FCSTD DOCUMENT  (FreeCAD 0.16R6712 (Git))
Label: parts
License: All rights reserved
LicenseURL: http://en.wikipedia.org/wiki/All_rights_reserved
objects: Part::Cylinder×41, Part::Cut×38, Part::Box×37, Part::MultiFuse×33, Part::Feature×31, Part::Fillet×30, Sketcher::SketchObject×22, PartDesign::Pad×21, Part::Chamfer×11, Part::Mirroring×6, Mesh::Feature×4, Part::Prism×3, Part::Thickness×2, App::DocumentObjectGroup×2, Part::FeaturePython×1, Part::Cone×1
note: 298 computed .brp shape members not serialized (recipe doc carries the construction recipe); baked Part::Feature solids carry a one-line shape summary decoded from their .brp

FEATURE [Part::Feature] Part__Feature  label="MEGAboard"
  shape: bbox 53.34 x 1.6 x 101.6 mm, 230 faces (baked)
FEATURE [Part::Feature] Part__Feature003  label="USB SHELL"
  Placement = pos=(-38.02,0.43,6.35) rot=(0,0,1;0rad)
  shape: bbox 13.78 x 15.2 x 16.51 mm, 218 faces (baked)
FEATURE [Part::MultiFuse] Fusion
  Placement = pos=(65,6,21) rot=(1,0,0;1.5708rad)
  Shapes = -> [Part__Feature,Part__Feature003]
FEATURE [Part::Box] Box  label="Cube"
  Height = 67
  Length = 84
  Placement = pos=(0,0,-3) rot=(0,0,1;0rad)
  Width = 120
FEATURE [Part::Box] Box001  label="Cube001"
  Height = 20
  Length = 20
  Placement = pos=(-20,0,0) rot=(0,0,-1;1.5708rad)
  Width = 300
FEATURE [Part::Box] Box002  label="Cube002"
  Height = 20
  Length = 20
  Placement = pos=(-20,0,50) rot=(0,0,-1;1.5708rad)
  Width = 300
FEATURE [Part::Box] Box003  label="Cube003"
  Height = 52
  Length = 54
  Placement = pos=(9,0,15) rot=(0,0,1;0rad)
  Width = 105
FEATURE [Part::Box] Box004  label="Cube004"
  Height = 20
  Length = 20
  Placement = pos=(-20,0,50) rot=(0,0,1;0rad)
  Width = 300
FEATURE [Part::Box] Box005  label="Cube005"
  Height = 20
  Length = 20
  Placement = pos=(-20,0,0) rot=(0,0,1;0rad)
  Width = 300
FEATURE [Sketcher::SketchObject] Sketch001
  Placement = pos=(0,0,100) rot=(0,0,1;0rad)
  sketch-geometry (28):
    g0: LineSegment StartX=82 StartY=111 StartZ=0 EndX=82 EndY=9 EndZ=0
    g1: LineSegment StartX=75 StartY=2 StartZ=0 EndX=9 EndY=2 EndZ=0
    g2: LineSegment StartX=2 StartY=9 StartZ=0 EndX=2 EndY=111 EndZ=0
    g3: ArcOfCircle CenterX=2 CenterY=118 CenterZ=0 NormalX=0 NormalY=0 NormalZ=1 Radius=7 StartAngle=4.71239 EndAngle=6.28319
    g4: LineSegment StartX=9 StartY=118 StartZ=0 EndX=75 EndY=118 EndZ=0
    g5: ArcOfCircle CenterX=2 CenterY=2 CenterZ=0 NormalX=0 NormalY=0 NormalZ=1 Radius=7 StartAngle=0 EndAngle=1.5708
    g6: ArcOfCircle CenterX=82 CenterY=2 CenterZ=0 NormalX=0 NormalY=0 NormalZ=1 Radius=7 StartAngle=1.5708 EndAngle=3.14159
    g7: ArcOfCircle CenterX=82 CenterY=118 CenterZ=0 NormalX=0 NormalY=0 NormalZ=1 Radius=7 StartAngle=3.14159 EndAngle=4.71239
    g8: LineSegment [constr] StartX=82 StartY=118 StartZ=0 EndX=75 EndY=118 EndZ=0
    g9: LineSegment [constr] StartX=82 StartY=118 StartZ=0 EndX=82 EndY=111 EndZ=0
    g10: LineSegment [constr] StartX=82 StartY=2 StartZ=0 EndX=82 EndY=9 EndZ=0
    g11: LineSegment [constr] StartX=82 StartY=2 StartZ=0 EndX=75 EndY=2 EndZ=0
    g12: LineSegment [constr] StartX=2 StartY=2 StartZ=0 EndX=2 EndY=9 EndZ=0
    g13: LineSegment [constr] StartX=2 StartY=2 StartZ=0 EndX=9 EndY=2 EndZ=0
    g14: LineSegment [constr] StartX=2 StartY=118 StartZ=0 EndX=2 EndY=111 EndZ=0
    g15: LineSegment [constr] StartX=2 StartY=118 StartZ=0 EndX=9 EndY=118 EndZ=0
    g16: Circle [constr] CenterX=4 CenterY=116 CenterZ=0 NormalX=0 NormalY=0 NormalZ=1 Radius=1.5
    g17: Circle [constr] CenterX=80 CenterY=116 CenterZ=0 NormalX=0 NormalY=0 NormalZ=1 Radius=1.5
    g18: Circle [constr] CenterX=80 CenterY=4 CenterZ=0 NormalX=0 NormalY=0 NormalZ=1 Radius=1.5
    g19: Circle [constr] CenterX=4 CenterY=4 CenterZ=0 NormalX=0 NormalY=0 NormalZ=1 Radius=1.5
    g20: LineSegment [constr] StartX=4 StartY=116 StartZ=0 EndX=80 EndY=116 EndZ=0
    g21: LineSegment [constr] StartX=80 StartY=116 StartZ=0 EndX=80 EndY=4 EndZ=0
    g22: LineSegment [constr] StartX=80 StartY=4 StartZ=0 EndX=4 EndY=4 EndZ=0
    g23: LineSegment [constr] StartX=4 StartY=4 StartZ=0 EndX=4 EndY=116 EndZ=0
    g24: LineSegment [constr] StartX=80 StartY=116 StartZ=0 EndX=80 EndY=118 EndZ=0
    g25: LineSegment [constr] StartX=80 StartY=116 StartZ=0 EndX=82 EndY=116 EndZ=0
    g26: LineSegment [constr] StartX=2 StartY=4 StartZ=0 EndX=4 EndY=4 EndZ=0
    g27: LineSegment [constr] StartX=4 StartY=4 StartZ=0 EndX=4 EndY=2 EndZ=0
  constraints (76):
    c: Horizontal(g1)
    c: Vertical(g0)
    c: Vertical(g2)
    c: Coincident(g4,g3)
    c: Coincident(g2,g3)
    c: Horizontal(g4)
    c: Coincident(g5,g2)
    c: Coincident(g5,g1)
    c: Coincident(g6,g0)
    c: Coincident(g6,g1)
    c: Coincident(g7,g4)
    c: Coincident(g7,g0)
    c: Coincident(g8,g7)
    c: Coincident(g8,g4)
    c: Coincident(g9,g7)
    c: Coincident(g9,g0)
    c: Coincident(g10,g6)
    c: Coincident(g10,g0)
    c: Vertical(g10)
    c: Coincident(g11,g6)
    c: Coincident(g11,g1)
    c: Horizontal(g11)
    c: Coincident(g12,g5)
    c: Coincident(g12,g2)
    c: Coincident(g13,g5)
    c: Coincident(g13,g1)
    c: Horizontal(g13)
    c: Horizontal(g8)
    c: Vertical(g9)
    c: Coincident(g14,g3)
    c: Coincident(g14,g2)
    c: Coincident(g15,g3)
    c: Coincident(g15,g3)
    c: Horizontal(g15)
    c: Vertical(g14)
    c: Distance(g3,g7) = 80
    c: Distance(g3,g5) = 116
    c: Vertical(g12)
    c: Equal(g3,g7)
    c: Equal(g7,g6)
    c: Equal(g6,g5)
    c: Radius(g5) = 7
    c: DistanceY(g-1,g5) = 2
    c: DistanceX(g-1,g5) = 2
    c: Coincident(g20,g21)
    c: Coincident(g21,g22)
    c: Coincident(g22,g23)
    c: Coincident(g23,g20)
    c: Horizontal(g20)
    c: Horizontal(g22)
    c: Vertical(g21)
    c: Vertical(g23)
    c: Coincident(g20,g16)
    c: Coincident(g21,g18)
    c: Coincident(g22,g19)
    c: Coincident(g20,g17)
    c: Radius(g17) = 1.5
    c: Equal(g17,g16)
    c: Equal(g17,g18)
    c: Equal(g17,g19)
    c: Coincident(g24,g17)
    c: PointOnObject(g24,g8)
    c: Coincident(g25,g17)
    c: PointOnObject(g25,g9)
    c: Horizontal(g25)
    c: Vertical(g24)
    c: PointOnObject(g26,g12)
    c: Coincident(g26,g19)
    c: Coincident(g26,g27)
    c: PointOnObject(g27,g13)
    c: Vertical(g27)
    c: Horizontal(g26)
    c: Equal(g26,g27)
    c: Equal(g27,g24)
    c: Equal(g24,g25)
    c: Distance(g26) = 2
FEATURE [Sketcher::SketchObject] Sketch002
  Placement = pos=(0,0,100) rot=(0,0,1;0rad)
  sketch-geometry (28):
    g0: LineSegment [constr] StartX=81 StartY=110 StartZ=0 EndX=81 EndY=10 EndZ=0
    g1: LineSegment [constr] StartX=74 StartY=3 StartZ=0 EndX=10 EndY=3 EndZ=0
    g2: LineSegment [constr] StartX=3 StartY=10 StartZ=0 EndX=3 EndY=110 EndZ=0
    g3: ArcOfCircle [constr] CenterX=3 CenterY=117 CenterZ=0 NormalX=0 NormalY=0 NormalZ=1 Radius=7 StartAngle=4.71239 EndAngle=6.28319
    g4: LineSegment [constr] StartX=10 StartY=117 StartZ=0 EndX=74 EndY=117 EndZ=0
    g5: ArcOfCircle [constr] CenterX=3 CenterY=3 CenterZ=0 NormalX=0 NormalY=0 NormalZ=1 Radius=7 StartAngle=0 EndAngle=1.5708
    g6: ArcOfCircle [constr] CenterX=81 CenterY=3 CenterZ=0 NormalX=0 NormalY=0 NormalZ=1 Radius=7 StartAngle=1.5708 EndAngle=3.14159
    g7: ArcOfCircle [constr] CenterX=81 CenterY=117 CenterZ=0 NormalX=0 NormalY=0 NormalZ=1 Radius=7 StartAngle=3.14159 EndAngle=4.71239
    g8: LineSegment [constr] StartX=81 StartY=117 StartZ=0 EndX=74 EndY=117 EndZ=0
    g9: LineSegment [constr] StartX=81 StartY=117 StartZ=0 EndX=81 EndY=110 EndZ=0
    g10: LineSegment [constr] StartX=81 StartY=3 StartZ=0 EndX=81 EndY=10 EndZ=0
    g11: LineSegment [constr] StartX=81 StartY=3 StartZ=0 EndX=74 EndY=3 EndZ=0
    g12: LineSegment [constr] StartX=3 StartY=3 StartZ=0 EndX=3 EndY=10 EndZ=0
    g13: LineSegment [constr] StartX=3 StartY=3 StartZ=0 EndX=10 EndY=3 EndZ=0
    g14: LineSegment [constr] StartX=3 StartY=117 StartZ=0 EndX=3 EndY=110 EndZ=0
    g15: LineSegment [constr] StartX=3 StartY=117 StartZ=0 EndX=10 EndY=117 EndZ=0
    g16: Circle CenterX=5 CenterY=115 CenterZ=0 NormalX=0 NormalY=0 NormalZ=1 Radius=1.5
    g17: Circle CenterX=79 CenterY=115 CenterZ=0 NormalX=0 NormalY=0 NormalZ=1 Radius=1.5
    g18: Circle CenterX=79 CenterY=5 CenterZ=0 NormalX=0 NormalY=0 NormalZ=1 Radius=1.5
    g19: Circle CenterX=5 CenterY=5 CenterZ=0 NormalX=0 NormalY=0 NormalZ=1 Radius=1.5
    g20: LineSegment [constr] StartX=5 StartY=115 StartZ=0 EndX=79 EndY=115 EndZ=0
    g21: LineSegment [constr] StartX=79 StartY=115 StartZ=0 EndX=79 EndY=5 EndZ=0
    g22: LineSegment [constr] StartX=79 StartY=5 StartZ=0 EndX=5 EndY=5 EndZ=0
    g23: LineSegment [constr] StartX=5 StartY=5 StartZ=0 EndX=5 EndY=115 EndZ=0
    g24: LineSegment [constr] StartX=79 StartY=115 StartZ=0 EndX=79 EndY=117 EndZ=0
    g25: LineSegment [constr] StartX=79 StartY=115 StartZ=0 EndX=81 EndY=115 EndZ=0
    g26: LineSegment [constr] StartX=3 StartY=5 StartZ=0 EndX=5 EndY=5 EndZ=0
    g27: LineSegment [constr] StartX=5 StartY=5 StartZ=0 EndX=5 EndY=3 EndZ=0
  constraints (76):
    c: Horizontal(g1)
    c: Vertical(g0)
    c: Vertical(g2)
    c: Coincident(g4,g3)
    c: Coincident(g2,g3)
    c: Horizontal(g4)
    c: Coincident(g5,g2)
    c: Coincident(g5,g1)
    c: Coincident(g6,g0)
    c: Coincident(g6,g1)
    c: Coincident(g7,g4)
    c: Coincident(g7,g0)
    c: Coincident(g8,g7)
    c: Coincident(g8,g4)
    c: Coincident(g9,g7)
    c: Coincident(g9,g0)
    c: Coincident(g10,g6)
    c: Coincident(g10,g0)
    c: Vertical(g10)
    c: Coincident(g11,g6)
    c: Coincident(g11,g1)
    c: Horizontal(g11)
    c: Coincident(g12,g5)
    c: Coincident(g12,g2)
    c: Coincident(g13,g5)
    c: Coincident(g13,g1)
    c: Horizontal(g13)
    c: Horizontal(g8)
    c: Vertical(g9)
    c: Coincident(g14,g3)
    c: Coincident(g14,g2)
    c: Coincident(g15,g3)
    c: Coincident(g15,g3)
    c: Horizontal(g15)
    c: Vertical(g14)
    c: Distance(g3,g7) = 78
    c: Distance(g3,g5) = 114
    c: Vertical(g12)
    c: Equal(g3,g7)
    c: Equal(g7,g6)
    c: Equal(g6,g5)
    c: Radius(g5) = 7
    c: DistanceY(g-1,g5) = 3
    c: DistanceX(g-1,g5) = 3
    c: Coincident(g20,g21)
    c: Coincident(g21,g22)
    c: Coincident(g22,g23)
    c: Coincident(g23,g20)
    c: Horizontal(g20)
    c: Horizontal(g22)
    c: Vertical(g21)
    c: Vertical(g23)
    c: Coincident(g20,g16)
    c: Coincident(g21,g18)
    c: Coincident(g22,g19)
    c: Coincident(g20,g17)
    c: Radius(g17) = 1.5
    c: Equal(g17,g16)
    c: Equal(g17,g18)
    c: Equal(g17,g19)
    c: Coincident(g24,g17)
    c: PointOnObject(g24,g8)
    c: Coincident(g25,g17)
    c: PointOnObject(g25,g9)
    c: Horizontal(g25)
    c: Vertical(g24)
    c: PointOnObject(g26,g12)
    c: Coincident(g26,g19)
    c: Coincident(g26,g27)
    c: PointOnObject(g27,g13)
    c: Vertical(g27)
    c: Horizontal(g26)
    c: Equal(g26,g27)
    c: Equal(g27,g24)
    c: Equal(g24,g25)
    c: Distance(g26) = 2
FEATURE [PartDesign::Pad] Pad
  Length = 101
  Length2 = 100
  Placement = pos=(0,0,100) rot=(0,0,1;0rad)
  Reversed = true
  Sketch = -> Sketch001
  Type = 0
FEATURE [Part::Cut] Cut
  Base = -> Box
  Tool = -> Pad
FEATURE [PartDesign::Pad] Pad001
  Length = 55
  Length2 = 100
  Placement = pos=(0,0,100) rot=(0,0,1;0rad)
  Reversed = true
  Sketch = -> Sketch002
  Type = 0
FEATURE [Part::Cut] Cut001
  Base = -> Cut
  Tool = -> Pad001
FEATURE [Part::Fillet] Fillet
  Base = -> Cut001
  Edges = 4 edges r=3: [Edge1,Edge3,Edge6,Edge23]
FEATURE [Part::Box] Box006  label="Cube006"
  Height = 14
  Length = 10
  Placement = pos=(80,11,3) rot=(0,0,1;0rad)
  Width = 32
FEATURE [Part::Fillet] Fillet001
  Base = -> Box006
  Edges = 4 edges r=1.5: [Edge9,Edge10,Edge11,Edge12]
FEATURE [Part::Fillet] Fillet002
  Base = -> Box006
  Edges = 4 edges r=1.5: [Edge9,Edge10,Edge11,Edge12]
  Placement = pos=(54,36,50) rot=(0,0,1;1.5708rad)
FEATURE [Part::Box] Box007  label="Cube007"
  Height = 12
  Length = 13
  Placement = pos=(20.5,-1,21) rot=(0,0,1;0rad)
  Width = 12
FEATURE [Part::Fillet] Fillet003
  Base = -> Box007
  Edges = 4 edges r=0.5: [Edge2,Edge4,Edge6,Edge8]
FEATURE [Sketcher::SketchObject] Sketch
  Placement = pos=(0,0,30) rot=(0,0,1;0rad)
  sketch-geometry (5):
    g0: Circle CenterX=29.4315 CenterY=72.043 CenterZ=0 NormalX=0 NormalY=0 NormalZ=1 Radius=1.5
    g1: Circle CenterX=57.3918 CenterY=72.0245 CenterZ=0 NormalX=0 NormalY=0 NormalZ=1 Radius=1.5
    g2: Circle CenterX=14.2201 CenterY=21.2508 CenterZ=0 NormalX=0 NormalY=0 NormalZ=1 Radius=1.5
    g3: Circle CenterX=62.4588 CenterY=102.502 CenterZ=0 NormalX=0 NormalY=0 NormalZ=1 Radius=1.5
    g4: Circle CenterX=62.4536 CenterY=19.9802 CenterZ=0 NormalX=0 NormalY=0 NormalZ=1 Radius=1.5
  constraints (5):
    c: Equal(g2,g4)
    c: Equal(g4,g1)
    c: Equal(g1,g3)
    c: Equal(g3,g0)
    c: Radius(g4) = 1.5
FEATURE [Sketcher::SketchObject] Sketch003
  Placement = pos=(0,0,-2) rot=(0,0,1;0rad)
  sketch-geometry (5):
    g0: Circle CenterX=29.4315 CenterY=72.043 CenterZ=0 NormalX=0 NormalY=0 NormalZ=1 Radius=3
    g1: Circle CenterX=57.3918 CenterY=72.0245 CenterZ=0 NormalX=0 NormalY=0 NormalZ=1 Radius=3
    g2: Circle CenterX=14.2201 CenterY=21.2508 CenterZ=0 NormalX=0 NormalY=0 NormalZ=1 Radius=3
    g3: Circle CenterX=62.4588 CenterY=102.502 CenterZ=0 NormalX=0 NormalY=0 NormalZ=1 Radius=3
    g4: Circle CenterX=62.4536 CenterY=19.9802 CenterZ=0 NormalX=0 NormalY=0 NormalZ=1 Radius=3
  constraints (5):
    c: Equal(g2,g4)
    c: Equal(g4,g1)
    c: Equal(g1,g3)
    c: Equal(g3,g0)
    c: Radius(g4) = 3
FEATURE [PartDesign::Pad] Pad002
  Length = 21.5
  Length2 = 100
  Placement = pos=(0,0,-2) rot=(0,0,1;0rad)
  Sketch = -> Sketch003
  Type = 0
FEATURE [Part::Box] Box008  label="Cube008"
  Height = 10
  Length = 6
  Placement = pos=(14,32,0) rot=(0,0,1;0rad)
  Width = 30
FEATURE [Part::Fillet] Fillet006
  Base = -> Box008
  Edges = 4 edges r=1: [Edge1,Edge3,Edge5,Edge7]
  Placement = pos=(0,0,-5) rot=(0,0,1;0rad)
FEATURE [Part::FeaturePython] Array  # Draft array (typed FeaturePython)
  Angle = 360
  ArrayType = 0
  Axis = (0,0,1)
  Base = -> Fillet006
  Center = (0,0,0)
  Fuse = false
  IntervalAxis = (0,0,0)
  IntervalX = (10,0,0)
  IntervalY = (0,1,0)
  IntervalZ = (0,0,0)
  NumberPolar = 1
  NumberX = 6
  NumberY = 1
  NumberZ = 1
FEATURE [PartDesign::Pad] Pad003
  Length = 20
  Length2 = 100
  Placement = pos=(0,0,30) rot=(0,0,1;0rad)
  Reversed = true
  Sketch = -> Sketch
  Type = 0
FEATURE [Part::Box] Box009  label="Cube009"
  Height = 3
  Length = 14
  Placement = pos=(-7,-17,-3) rot=(0,0,1;0rad)
  Width = 18
FEATURE [Part::Cylinder] Cylinder
  Angle = 360
  Height = 10
  Placement = pos=(0,-10,-5) rot=(0,0,1;0rad)
  Radius = 2.1
FEATURE [Part::Fillet] Fillet007
  Base = -> Box009
  Edges = 2 edges r=4: [Edge1,Edge5]
FEATURE [Part::Cut] Cut006
  Base = -> Fillet007
  Placement = pos=(16,0,0) rot=(0,0,1;0rad)
  Tool = -> Cylinder
FEATURE [Part::Cut] Cut007
  Base = -> Fillet007
  Placement = pos=(68,0,0) rot=(0,0,1;0rad)
  Tool = -> Cylinder
FEATURE [Part::Cut] Cut008
  Base = -> Fillet007
  Placement = pos=(0,40,0) rot=(0,0,-1;1.5708rad)
  Tool = -> Cylinder
FEATURE [Part::Cut] Cut009
  Base = -> Fillet007
  Placement = pos=(0,104,0) rot=(0,0,-1;1.5708rad)
  Tool = -> Cylinder
FEATURE [Part::Fillet] Fillet008
  Base = -> Box006
  Edges = 4 edges r=1.5: [Edge9,Edge10,Edge11,Edge12]
  Placement = pos=(54,36,0) rot=(0,0,1;1.5708rad)
FEATURE [Part::MultiFuse] Fusion001
  Shapes = -> [Fillet002,Fillet008,Fillet001]
FEATURE [Part::Cut] Cut010
  Base = -> Fillet
  Tool = -> Fusion001
FEATURE [Part::MultiFuse] Fusion002
  Shapes = -> [Cut007,Cut006,Cut008,Cut009]
FEATURE [Part::Cut] Cut011
  Base = -> Cut010
  Tool = -> Fillet003
FEATURE [Part::Cut] Cut012
  Base = -> Cut011
  Tool = -> Array
FEATURE [Part::MultiFuse] Fusion003
  Shapes = -> [Cut012,Pad002]
FEATURE [Part::Cut] Cut013
  Base = -> Fusion003
  Tool = -> Pad003
FEATURE [Part::Fillet] Fillet009
  Base = -> Cut013
  Edges = 8 edges r=1.5: [Edge106,Edge116,Edge118,Edge120,Edge123,Edge132,Edge135,Edge144]
FEATURE [Part::Fillet] Fillet010
  Base = -> Fillet009
  Edges = 5 edges r=3: [Edge92,Edge93,Edge142,Edge143,Edge144]
FEATURE [Part::MultiFuse] Fusion004
  Shapes = -> [Fillet010,Fusion002]
FEATURE [Sketcher::SketchObject] Sketch006
  Placement = pos=(0,0,1) rot=(0,0,1;0rad)
  sketch-geometry (35):
    g0: LineSegment StartX=-33.3333 StartY=25 StartZ=0 EndX=-16.6667 EndY=25 EndZ=0
    g1: LineSegment StartX=-16.6667 StartY=25 StartZ=0 EndX=-16.6667 EndY=-25 EndZ=0
    g2: LineSegment StartX=-16.6667 StartY=-25 StartZ=0 EndX=-33.3333 EndY=-25 EndZ=0
    g3: LineSegment StartX=-33.3333 StartY=-25 StartZ=0 EndX=-33.3333 EndY=25 EndZ=0
    g4: LineSegment StartX=-8.33333 StartY=-25 StartZ=0 EndX=8.33333 EndY=-25 EndZ=0
    g5: LineSegment StartX=8.33333 StartY=-25 StartZ=0 EndX=8.33333 EndY=-8.33333 EndZ=0
    g6: LineSegment StartX=8.33333 StartY=-8.33333 StartZ=0 EndX=16.6667 EndY=-8.33333 EndZ=0
    g7: LineSegment StartX=16.6667 StartY=-8.33333 StartZ=0 EndX=16.6667 EndY=-25 EndZ=0
    g8: LineSegment StartX=16.6667 StartY=-25 StartZ=0 EndX=33.3333 EndY=-25 EndZ=0
    g9: LineSegment StartX=33.3333 StartY=-25 StartZ=0 EndX=33.3333 EndY=25 EndZ=0
    g10: LineSegment StartX=16.6667 StartY=25 StartZ=0 EndX=16.6667 EndY=8.33333 EndZ=0
    g11: LineSegment StartX=8.33333 StartY=8.33333 StartZ=0 EndX=8.33333 EndY=25 EndZ=0
    g12: LineSegment StartX=8.33333 StartY=25 StartZ=0 EndX=-8.33333 EndY=25 EndZ=0
    g13: LineSegment [constr] StartX=16.6667 StartY=8.33333 StartZ=0 EndX=16.6667 EndY=-8.33333 EndZ=0
    g14: LineSegment StartX=8.33333 StartY=8.33333 StartZ=0 EndX=16.6667 EndY=8.33333 EndZ=0
    g15: LineSegment [constr] StartX=-16.6667 StartY=25 StartZ=0 EndX=-8.33333 EndY=25 EndZ=0
    g16: LineSegment [constr] StartX=8.33333 StartY=25 StartZ=0 EndX=16.6667 EndY=25 EndZ=0
    g17: LineSegment StartX=-8.33333 StartY=25 StartZ=0 EndX=-8.33333 EndY=8.33333 EndZ=0
    g18: LineSegment StartX=-8.33333 StartY=8.33333 StartZ=0 EndX=-12.5 EndY=8.33333 EndZ=0
    g19: LineSegment StartX=-12.5 StartY=8.33333 StartZ=0 EndX=-12.5 EndY=-8.33333 EndZ=0
    g20: LineSegment StartX=-12.5 StartY=-8.33333 StartZ=0 EndX=-8.33333 EndY=-8.33333 EndZ=0
    g21: LineSegment StartX=-8.33333 StartY=-8.33333 StartZ=0 EndX=-8.33333 EndY=-25 EndZ=0
    g22: LineSegment [constr] StartX=-8.33333 StartY=8.33333 StartZ=0 EndX=-8.33333 EndY=-8.33333 EndZ=0
    g23: LineSegment [constr] StartX=-16.6667 StartY=8.33333 StartZ=0 EndX=-12.5 EndY=8.33333 EndZ=0
    g24: LineSegment StartX=16.6667 StartY=25 StartZ=0 EndX=25 EndY=25 EndZ=0
    g25: LineSegment StartX=25 StartY=25 StartZ=0 EndX=33.3333 EndY=25 EndZ=0
    g26: LineSegment [constr] StartX=8.33333 StartY=8.33333 StartZ=0 EndX=8.33333 EndY=-8.33333 EndZ=0
    g27: LineSegment [constr] StartX=-16.6667 StartY=-25 StartZ=0 EndX=-8.33333 EndY=-25 EndZ=0
    g28: Circle CenterX=-25 CenterY=16.6667 CenterZ=0 NormalX=0 NormalY=0 NormalZ=1 Radius=4.16667
    g29: LineSegment [constr] StartX=-33.3333 StartY=25 StartZ=0 EndX=-25 EndY=16.6667 EndZ=0
    g30: LineSegment [constr] StartX=-25 StartY=16.6667 StartZ=0 EndX=-16.6667 EndY=25 EndZ=0
    g31: LineSegment [constr] StartX=-33.3333 StartY=16.6667 StartZ=0 EndX=-29.1667 EndY=16.6667 EndZ=0
    g32: LineSegment [constr] StartX=-29.1667 StartY=16.6667 StartZ=0 EndX=-25 EndY=16.6667 EndZ=0
    g33: LineSegment [constr] StartX=-33.3333 StartY=-25 StartZ=0 EndX=0 EndY=0 EndZ=0
    g34: LineSegment [constr] StartX=0 StartY=0 StartZ=0 EndX=33.3333 EndY=25 EndZ=0
  constraints (95):
    c: Coincident(g0,g1)
    c: Coincident(g1,g2)
    c: Coincident(g2,g3)
    c: Coincident(g3,g0)
    c: Horizontal(g0)
    c: Horizontal(g2)
    c: Vertical(g1)
    c: Vertical(g3)
    c: Horizontal(g4)
    c: Coincident(g4,g5)
    c: Vertical(g5)
    c: Coincident(g5,g6)
    c: Horizontal(g6)
    c: Coincident(g6,g7)
    c: Vertical(g7)
    c: Coincident(g7,g8)
    c: Horizontal(g8)
    c: Coincident(g8,g9)
    c: Vertical(g9)
    c: Vertical(g11)
    c: Coincident(g11,g12)
    c: Horizontal(g12)
    c: Vertical(g10)
    c: Coincident(g13,g6)
    c: Vertical(g13)
    c: Coincident(g13,g10)
    c: Equal(g11,g12)
    c: Equal(g12,g0)
    c: Coincident(g14,g10)
    c: Horizontal(g14)
    c: Coincident(g11,g14)
    c: Coincident(g15,g0)
    c: Equal(g15,g14)
    c: Horizontal(g15)
    c: Coincident(g16,g11)
    c: Horizontal(g16)
    c: Coincident(g12,g17)
    c: Vertical(g17)
    c: Coincident(g17,g18)
    c: Horizontal(g18)
    c: Coincident(g18,g19)
    c: Vertical(g19)
    c: Coincident(g19,g20)
    c: Coincident(g20,g21)
    c: Coincident(g21,g4)
    c: Vertical(g21)
    c: Horizontal(g20)
    c: Coincident(g22,g17)
    c: Coincident(g22,g20)
    c: Vertical(g22)
    c: PointOnObject(g23,g1)
    c: Coincident(g23,g18)
    c: Horizontal(g23)
    c: Equal(g18,g23)
    c: Coincident(g10,g24)
    c: Horizontal(g24)
    c: Coincident(g24,g25)
    c: Coincident(g25,g9)
    c: Horizontal(g25)
    c: Equal(g16,g24)
    c: Equal(g24,g25)
    c: Coincident(g10,g16)
    c: Coincident(g15,g12)
    c: Equal(g17,g11)
    c: Equal(g7,g5)
    c: Equal(g21,g17)
    c: Coincident(g26,g11)
    c: Coincident(g26,g5)
    c: Vertical(g26)
    c: Coincident(g27,g1)
    c: Coincident(g27,g4)
    c: Horizontal(g27)
    c: Equal(g19,g17)
    c: Equal(g26,g11)
    c: Coincident(g29,g0)
    c: Coincident(g29,g28)
    c: Coincident(g30,g28)
    c: Coincident(g30,g0)
    c: Perpendicular(g30,g29)
    c: Equal(g30,g29)
    c: PointOnObject(g31,g3)
    c: PointOnObject(g31,g28)
    c: Coincident(g32,g31)
    c: Coincident(g32,g28)
    c: Horizontal(g31)
    c: Horizontal(g32)
    c: Equal(g31,g32)
    c: Equal(g4,g8)
    c: Distance(g3) = 50
    c: Coincident(g33,g2)
    c: Coincident(g33,g-1)
    c: Coincident(g34,g-1)
    c: Coincident(g34,g9)
    c: Parallel(g34,g33)
    c: Equal(g34,g33)
FEATURE [Sketcher::SketchObject] Sketch007
  sketch-geometry (16):
    g0: LineSegment StartX=-90 StartY=-35 StartZ=0 EndX=90 EndY=-35 EndZ=0
    g1: LineSegment StartX=90 StartY=-35 StartZ=0 EndX=90 EndY=35 EndZ=0
    g2: LineSegment StartX=90 StartY=35 StartZ=0 EndX=-90 EndY=35 EndZ=0
    g3: LineSegment StartX=-90 StartY=35 StartZ=0 EndX=-90 EndY=-35 EndZ=0
    g4: Circle CenterX=-80 CenterY=25 CenterZ=0 NormalX=0 NormalY=0 NormalZ=1 Radius=2
    g5: Circle CenterX=-80 CenterY=-25 CenterZ=0 NormalX=0 NormalY=0 NormalZ=1 Radius=2
    g6: Circle CenterX=80 CenterY=25 CenterZ=0 NormalX=0 NormalY=0 NormalZ=1 Radius=2
    g7: Circle CenterX=80 CenterY=-25 CenterZ=0 NormalX=0 NormalY=0 NormalZ=1 Radius=2
    g8: LineSegment [constr] StartX=80 StartY=25 StartZ=0 EndX=-80 EndY=25 EndZ=0
    g9: LineSegment [constr] StartX=-80 StartY=25 StartZ=0 EndX=-80 EndY=-25 EndZ=0
    g10: LineSegment [constr] StartX=-80 StartY=-25 StartZ=0 EndX=80 EndY=-25 EndZ=0
    g11: LineSegment [constr] StartX=80 StartY=-25 StartZ=0 EndX=80 EndY=25 EndZ=0
    g12: LineSegment [constr] StartX=-80 StartY=-25 StartZ=0 EndX=0 EndY=0 EndZ=0
    g13: LineSegment [constr] StartX=0 StartY=0 StartZ=0 EndX=80 EndY=25 EndZ=0
    g14: LineSegment [constr] StartX=80 StartY=25 StartZ=0 EndX=80 EndY=35 EndZ=0
    g15: LineSegment [constr] StartX=80 StartY=25 StartZ=0 EndX=90 EndY=25 EndZ=0
  constraints (40):
    c: Coincident(g0,g1)
    c: Coincident(g1,g2)
    c: Coincident(g2,g3)
    c: Coincident(g3,g0)
    c: Horizontal(g0)
    c: Vertical(g1)
    c: Distance(g3) = 70
    c: Distance(g2) = 180
    c: Radius(g4) = 2
    c: Equal(g4,g5)
    c: Equal(g4,g6)
    c: Equal(g4,g7)
    c: Coincident(g8,g9)
    c: Coincident(g9,g10)
    c: Coincident(g10,g11)
    c: Coincident(g11,g8)
    c: Horizontal(g8)
    c: Horizontal(g10)
    c: Vertical(g9)
    c: Vertical(g11)
    c: Coincident(g8,g6)
    c: Coincident(g9,g5)
    c: Coincident(g4,g8)
    c: Coincident(g7,g10)
    c: Symmetric(g2,g1,g-2)
    c: Symmetric(g0,g2,g-1)
    c: Coincident(g12,g5)
    c: Coincident(g12,g-1)
    c: Coincident(g13,g-1)
    c: Coincident(g13,g6)
    c: Equal(g13,g12)
    c: Parallel(g12,g13)
    c: Distance(g11) = 50
    c: Coincident(g14,g6)
    c: PointOnObject(g14,g2)
    c: Vertical(g14)
    c: Coincident(g15,g6)
    c: PointOnObject(g15,g1)
    c: Horizontal(g15)
    c: Equal(g14,g15)
FEATURE [PartDesign::Pad] Pad004
  Length = 3
  Length2 = 100
  Sketch = -> Sketch007
  Type = 0
FEATURE [PartDesign::Pad] Pad005
  Length = 10
  Length2 = 100
  Placement = pos=(0,0,1) rot=(0,0,1;0rad)
  Sketch = -> Sketch006
  Type = 0
FEATURE [Part::Fillet] Fillet011
  Base = -> Pad004
  Edges = 4 edges r=3: [Edge1,Edge2,Edge5,Edge8]
FEATURE [Sketcher::SketchObject] Sketch008
  Placement = pos=(0,0,1.5) rot=(0,0,1;0rad)
  sketch-geometry (35):
    g0: LineSegment StartX=-33.3333 StartY=25 StartZ=0 EndX=-16.6667 EndY=25 EndZ=0
    g1: LineSegment StartX=-16.6667 StartY=25 StartZ=0 EndX=-16.6667 EndY=-25 EndZ=0
    g2: LineSegment StartX=-16.6667 StartY=-25 StartZ=0 EndX=-33.3333 EndY=-25 EndZ=0
    g3: LineSegment StartX=-33.3333 StartY=-25 StartZ=0 EndX=-33.3333 EndY=25 EndZ=0
    g4: LineSegment StartX=-8.33333 StartY=-25 StartZ=0 EndX=8.33333 EndY=-25 EndZ=0
    g5: LineSegment StartX=8.33333 StartY=-25 StartZ=0 EndX=8.33333 EndY=-8.33333 EndZ=0
    g6: LineSegment StartX=8.33333 StartY=-8.33333 StartZ=0 EndX=16.6667 EndY=-8.33333 EndZ=0
    g7: LineSegment StartX=16.6667 StartY=-8.33333 StartZ=0 EndX=16.6667 EndY=-25 EndZ=0
    g8: LineSegment StartX=16.6667 StartY=-25 StartZ=0 EndX=33.3333 EndY=-25 EndZ=0
    g9: LineSegment StartX=33.3333 StartY=-25 StartZ=0 EndX=33.3333 EndY=25 EndZ=0
    g10: LineSegment StartX=16.6667 StartY=25 StartZ=0 EndX=16.6667 EndY=8.33333 EndZ=0
    g11: LineSegment StartX=8.33333 StartY=8.33333 StartZ=0 EndX=8.33333 EndY=25 EndZ=0
    g12: LineSegment StartX=8.33333 StartY=25 StartZ=0 EndX=-8.33333 EndY=25 EndZ=0
    g13: LineSegment [constr] StartX=16.6667 StartY=8.33333 StartZ=0 EndX=16.6667 EndY=-8.33333 EndZ=0
    g14: LineSegment StartX=8.33333 StartY=8.33333 StartZ=0 EndX=16.6667 EndY=8.33333 EndZ=0
    g15: LineSegment [constr] StartX=-16.6667 StartY=25 StartZ=0 EndX=-8.33333 EndY=25 EndZ=0
    g16: LineSegment [constr] StartX=8.33333 StartY=25 StartZ=0 EndX=16.6667 EndY=25 EndZ=0
    g17: LineSegment StartX=-8.33333 StartY=25 StartZ=0 EndX=-8.33333 EndY=8.33333 EndZ=0
    g18: LineSegment StartX=-8.33333 StartY=8.33333 StartZ=0 EndX=-12.5 EndY=8.33333 EndZ=0
    g19: LineSegment StartX=-12.5 StartY=8.33333 StartZ=0 EndX=-12.5 EndY=-8.33333 EndZ=0
    g20: LineSegment StartX=-12.5 StartY=-8.33333 StartZ=0 EndX=-8.33333 EndY=-8.33333 EndZ=0
    g21: LineSegment StartX=-8.33333 StartY=-8.33333 StartZ=0 EndX=-8.33333 EndY=-25 EndZ=0
    g22: LineSegment [constr] StartX=-8.33333 StartY=8.33333 StartZ=0 EndX=-8.33333 EndY=-8.33333 EndZ=0
    g23: LineSegment [constr] StartX=-16.6667 StartY=8.33333 StartZ=0 EndX=-12.5 EndY=8.33333 EndZ=0
    g24: LineSegment StartX=16.6667 StartY=25 StartZ=0 EndX=25 EndY=25 EndZ=0
    g25: LineSegment StartX=25 StartY=25 StartZ=0 EndX=33.3333 EndY=25 EndZ=0
    g26: LineSegment [constr] StartX=8.33333 StartY=8.33333 StartZ=0 EndX=8.33333 EndY=-8.33333 EndZ=0
    g27: LineSegment [constr] StartX=-16.6667 StartY=-25 StartZ=0 EndX=-8.33333 EndY=-25 EndZ=0
    g28: Circle CenterX=-25 CenterY=16.6667 CenterZ=0 NormalX=0 NormalY=0 NormalZ=1 Radius=4.16667
    g29: LineSegment [constr] StartX=-33.3333 StartY=25 StartZ=0 EndX=-25 EndY=16.6667 EndZ=0
    g30: LineSegment [constr] StartX=-25 StartY=16.6667 StartZ=0 EndX=-16.6667 EndY=25 EndZ=0
    g31: LineSegment [constr] StartX=-33.3333 StartY=16.6667 StartZ=0 EndX=-29.1667 EndY=16.6667 EndZ=0
    g32: LineSegment [constr] StartX=-29.1667 StartY=16.6667 StartZ=0 EndX=-25 EndY=16.6667 EndZ=0
    g33: LineSegment [constr] StartX=-33.3333 StartY=-25 StartZ=0 EndX=0 EndY=0 EndZ=0
    g34: LineSegment [constr] StartX=0 StartY=0 StartZ=0 EndX=33.3333 EndY=25 EndZ=0
  constraints (95):
    c: Coincident(g0,g1)
    c: Coincident(g1,g2)
    c: Coincident(g2,g3)
    c: Coincident(g3,g0)
    c: Horizontal(g0)
    c: Horizontal(g2)
    c: Vertical(g1)
    c: Vertical(g3)
    c: Horizontal(g4)
    c: Coincident(g4,g5)
    c: Vertical(g5)
    c: Coincident(g5,g6)
    c: Horizontal(g6)
    c: Coincident(g6,g7)
    c: Vertical(g7)
    c: Coincident(g7,g8)
    c: Horizontal(g8)
    c: Coincident(g8,g9)
    c: Vertical(g9)
    c: Vertical(g11)
    c: Coincident(g11,g12)
    c: Horizontal(g12)
    c: Vertical(g10)
    c: Coincident(g13,g6)
    c: Vertical(g13)
    c: Coincident(g13,g10)
    c: Equal(g11,g12)
    c: Equal(g12,g0)
    c: Coincident(g14,g10)
    c: Horizontal(g14)
    c: Coincident(g11,g14)
    c: Coincident(g15,g0)
    c: Equal(g15,g14)
    c: Horizontal(g15)
    c: Coincident(g16,g11)
    c: Horizontal(g16)
    c: Coincident(g12,g17)
    c: Vertical(g17)
    c: Coincident(g17,g18)
    c: Horizontal(g18)
    c: Coincident(g18,g19)
    c: Vertical(g19)
    c: Coincident(g19,g20)
    c: Coincident(g20,g21)
    c: Coincident(g21,g4)
    c: Vertical(g21)
    c: Horizontal(g20)
    c: Coincident(g22,g17)
    c: Coincident(g22,g20)
    c: Vertical(g22)
    c: PointOnObject(g23,g1)
    c: Coincident(g23,g18)
    c: Horizontal(g23)
    c: Equal(g18,g23)
    c: Coincident(g10,g24)
    c: Horizontal(g24)
    c: Coincident(g24,g25)
    c: Coincident(g25,g9)
    c: Horizontal(g25)
    c: Equal(g16,g24)
    c: Equal(g24,g25)
    c: Coincident(g10,g16)
    c: Coincident(g15,g12)
    c: Equal(g17,g11)
    c: Equal(g7,g5)
    c: Equal(g21,g17)
    c: Coincident(g26,g11)
    c: Coincident(g26,g5)
    c: Vertical(g26)
    c: Coincident(g27,g1)
    c: Coincident(g27,g4)
    c: Horizontal(g27)
    c: Equal(g19,g17)
    c: Equal(g26,g11)
    c: Coincident(g29,g0)
    c: Coincident(g29,g28)
    c: Coincident(g30,g28)
    c: Coincident(g30,g0)
    c: Perpendicular(g30,g29)
    c: Equal(g30,g29)
    c: PointOnObject(g31,g3)
    c: PointOnObject(g31,g28)
    c: Coincident(g32,g31)
    c: Coincident(g32,g28)
    c: Horizontal(g31)
    c: Horizontal(g32)
    c: Equal(g31,g32)
    c: Equal(g4,g8)
    c: Distance(g3) = 50
    c: Coincident(g33,g2)
    c: Coincident(g33,g-1)
    c: Coincident(g34,g-1)
    c: Coincident(g34,g9)
    c: Parallel(g34,g33)
    c: Equal(g34,g33)
FEATURE [PartDesign::Pad] Pad006
  Length = 2
  Length2 = 100
  Placement = pos=(0,0,1.5) rot=(0,0,1;0rad)
  Sketch = -> Sketch008
  Type = 0
FEATURE [Sketcher::SketchObject] Sketch009
  Placement = pos=(0,0,100) rot=(0,0,1;0rad)
  sketch-geometry (28):
    g0: LineSegment [constr] StartX=81 StartY=110 StartZ=0 EndX=81 EndY=10 EndZ=0
    g1: LineSegment [constr] StartX=74 StartY=3 StartZ=0 EndX=10 EndY=3 EndZ=0
    g2: LineSegment [constr] StartX=3 StartY=10 StartZ=0 EndX=3 EndY=110 EndZ=0
    g3: ArcOfCircle [constr] CenterX=3 CenterY=117 CenterZ=0 NormalX=0 NormalY=0 NormalZ=1 Radius=7 StartAngle=4.71239 EndAngle=6.28319
    g4: LineSegment [constr] StartX=10 StartY=117 StartZ=0 EndX=74 EndY=117 EndZ=0
    g5: ArcOfCircle [constr] CenterX=3 CenterY=3 CenterZ=0 NormalX=0 NormalY=0 NormalZ=1 Radius=7 StartAngle=0 EndAngle=1.5708
    g6: ArcOfCircle [constr] CenterX=81 CenterY=3 CenterZ=0 NormalX=0 NormalY=0 NormalZ=1 Radius=7 StartAngle=1.5708 EndAngle=3.14159
    g7: ArcOfCircle [constr] CenterX=81 CenterY=117 CenterZ=0 NormalX=0 NormalY=0 NormalZ=1 Radius=7 StartAngle=3.14159 EndAngle=4.71239
    g8: LineSegment [constr] StartX=81 StartY=117 StartZ=0 EndX=74 EndY=117 EndZ=0
    g9: LineSegment [constr] StartX=81 StartY=117 StartZ=0 EndX=81 EndY=110 EndZ=0
    g10: LineSegment [constr] StartX=81 StartY=3 StartZ=0 EndX=81 EndY=10 EndZ=0
    g11: LineSegment [constr] StartX=81 StartY=3 StartZ=0 EndX=74 EndY=3 EndZ=0
    g12: LineSegment [constr] StartX=3 StartY=3 StartZ=0 EndX=3 EndY=10 EndZ=0
    g13: LineSegment [constr] StartX=3 StartY=3 StartZ=0 EndX=10 EndY=3 EndZ=0
    g14: LineSegment [constr] StartX=3 StartY=117 StartZ=0 EndX=3 EndY=110 EndZ=0
    g15: LineSegment [constr] StartX=3 StartY=117 StartZ=0 EndX=10 EndY=117 EndZ=0
    g16: Circle CenterX=5 CenterY=115 CenterZ=0 NormalX=0 NormalY=0 NormalZ=1 Radius=1.65
    g17: Circle CenterX=79 CenterY=115 CenterZ=0 NormalX=0 NormalY=0 NormalZ=1 Radius=1.65
    g18: Circle CenterX=79 CenterY=5 CenterZ=0 NormalX=0 NormalY=0 NormalZ=1 Radius=1.65
    g19: Circle CenterX=5 CenterY=5 CenterZ=0 NormalX=0 NormalY=0 NormalZ=1 Radius=1.65
    g20: LineSegment [constr] StartX=5 StartY=115 StartZ=0 EndX=79 EndY=115 EndZ=0
    g21: LineSegment [constr] StartX=79 StartY=115 StartZ=0 EndX=79 EndY=5 EndZ=0
    g22: LineSegment [constr] StartX=79 StartY=5 StartZ=0 EndX=5 EndY=5 EndZ=0
    g23: LineSegment [constr] StartX=5 StartY=5 StartZ=0 EndX=5 EndY=115 EndZ=0
    g24: LineSegment [constr] StartX=79 StartY=115 StartZ=0 EndX=79 EndY=117 EndZ=0
    g25: LineSegment [constr] StartX=79 StartY=115 StartZ=0 EndX=81 EndY=115 EndZ=0
    g26: LineSegment [constr] StartX=3 StartY=5 StartZ=0 EndX=5 EndY=5 EndZ=0
    g27: LineSegment [constr] StartX=5 StartY=5 StartZ=0 EndX=5 EndY=3 EndZ=0
  constraints (76):
    c: Horizontal(g1)
    c: Vertical(g0)
    c: Vertical(g2)
    c: Coincident(g4,g3)
    c: Coincident(g2,g3)
    c: Horizontal(g4)
    c: Coincident(g5,g2)
    c: Coincident(g5,g1)
    c: Coincident(g6,g0)
    c: Coincident(g6,g1)
    c: Coincident(g7,g4)
    c: Coincident(g7,g0)
    c: Coincident(g8,g7)
    c: Coincident(g8,g4)
    c: Coincident(g9,g7)
    c: Coincident(g9,g0)
    c: Coincident(g10,g6)
    c: Coincident(g10,g0)
    c: Vertical(g10)
    c: Coincident(g11,g6)
    c: Coincident(g11,g1)
    c: Horizontal(g11)
    c: Coincident(g12,g5)
    c: Coincident(g12,g2)
    c: Coincident(g13,g5)
    c: Coincident(g13,g1)
    c: Horizontal(g13)
    c: Horizontal(g8)
    c: Vertical(g9)
    c: Coincident(g14,g3)
    c: Coincident(g14,g2)
    c: Coincident(g15,g3)
    c: Coincident(g15,g3)
    c: Horizontal(g15)
    c: Vertical(g14)
    c: Distance(g3,g7) = 78
    c: Distance(g3,g5) = 114
    c: Vertical(g12)
    c: Equal(g3,g7)
    c: Equal(g7,g6)
    c: Equal(g6,g5)
    c: Radius(g5) = 7
    c: DistanceY(g-1,g5) = 3
    c: DistanceX(g-1,g5) = 3
    c: Coincident(g20,g21)
    c: Coincident(g21,g22)
    c: Coincident(g22,g23)
    c: Coincident(g23,g20)
    c: Horizontal(g20)
    c: Horizontal(g22)
    c: Vertical(g21)
    c: Vertical(g23)
    c: Coincident(g20,g16)
    c: Coincident(g21,g18)
    c: Coincident(g22,g19)
    c: Coincident(g20,g17)
    c: Radius(g17) = 1.65
    c: Equal(g17,g16)
    c: Equal(g17,g18)
    c: Equal(g17,g19)
    c: Coincident(g24,g17)
    c: PointOnObject(g24,g8)
    c: Coincident(g25,g17)
    c: PointOnObject(g25,g9)
    c: Horizontal(g25)
    c: Vertical(g24)
    c: PointOnObject(g26,g12)
    c: Coincident(g26,g19)
    c: Coincident(g26,g27)
    c: PointOnObject(g27,g13)
    c: Vertical(g27)
    c: Horizontal(g26)
    c: Equal(g26,g27)
    c: Equal(g27,g24)
    c: Equal(g24,g25)
    c: Distance(g26) = 2
FEATURE [PartDesign::Pad] Pad007
  Length = 55
  Length2 = 100
  Placement = pos=(0,0,100) rot=(0,0,1;0rad)
  Reversed = true
  Sketch = -> Sketch009
  Type = 0
FEATURE [Part::Box] Box010  label="Cube010"
  Height = 5
  Length = 84
  Placement = pos=(0,0,64) rot=(0,0,1;0rad)
  Width = 120
FEATURE [Part::Fillet] Fillet012
  Base = -> Box010
  Edges = 4 edges r=3: [Edge1,Edge3,Edge5,Edge7]
FEATURE [Sketcher::SketchObject] Sketch010
  Placement = pos=(0,0,68) rot=(0,0,1;0rad)
  sketch-geometry (28):
    g0: LineSegment StartX=82 StartY=111 StartZ=0 EndX=82 EndY=9 EndZ=0
    g1: LineSegment StartX=75 StartY=2 StartZ=0 EndX=9 EndY=2 EndZ=0
    g2: LineSegment StartX=2 StartY=9 StartZ=0 EndX=2 EndY=111 EndZ=0
    g3: ArcOfCircle CenterX=2 CenterY=118 CenterZ=0 NormalX=0 NormalY=0 NormalZ=1 Radius=7 StartAngle=4.71239 EndAngle=6.28319
    g4: LineSegment StartX=9 StartY=118 StartZ=0 EndX=75 EndY=118 EndZ=0
    g5: ArcOfCircle CenterX=2 CenterY=2 CenterZ=0 NormalX=0 NormalY=0 NormalZ=1 Radius=7 StartAngle=0 EndAngle=1.5708
    g6: ArcOfCircle CenterX=82 CenterY=2 CenterZ=0 NormalX=0 NormalY=0 NormalZ=1 Radius=7 StartAngle=1.5708 EndAngle=3.14159
    g7: ArcOfCircle CenterX=82 CenterY=118 CenterZ=0 NormalX=0 NormalY=0 NormalZ=1 Radius=7 StartAngle=3.14159 EndAngle=4.71239
    g8: LineSegment [constr] StartX=82 StartY=118 StartZ=0 EndX=75 EndY=118 EndZ=0
    g9: LineSegment [constr] StartX=82 StartY=118 StartZ=0 EndX=82 EndY=111 EndZ=0
    g10: LineSegment [constr] StartX=82 StartY=2 StartZ=0 EndX=82 EndY=9 EndZ=0
    g11: LineSegment [constr] StartX=82 StartY=2 StartZ=0 EndX=75 EndY=2 EndZ=0
    g12: LineSegment [constr] StartX=2 StartY=2 StartZ=0 EndX=2 EndY=9 EndZ=0
    g13: LineSegment [constr] StartX=2 StartY=2 StartZ=0 EndX=9 EndY=2 EndZ=0
    g14: LineSegment [constr] StartX=2 StartY=118 StartZ=0 EndX=2 EndY=111 EndZ=0
    g15: LineSegment [constr] StartX=2 StartY=118 StartZ=0 EndX=9 EndY=118 EndZ=0
    g16: Circle [constr] CenterX=4 CenterY=116 CenterZ=0 NormalX=0 NormalY=0 NormalZ=1 Radius=1.5
    g17: Circle [constr] CenterX=80 CenterY=116 CenterZ=0 NormalX=0 NormalY=0 NormalZ=1 Radius=1.5
    g18: Circle [constr] CenterX=80 CenterY=4 CenterZ=0 NormalX=0 NormalY=0 NormalZ=1 Radius=1.5
    g19: Circle [constr] CenterX=4 CenterY=4 CenterZ=0 NormalX=0 NormalY=0 NormalZ=1 Radius=1.5
    g20: LineSegment [constr] StartX=4 StartY=116 StartZ=0 EndX=80 EndY=116 EndZ=0
    g21: LineSegment [constr] StartX=80 StartY=116 StartZ=0 EndX=80 EndY=4 EndZ=0
    g22: LineSegment [constr] StartX=80 StartY=4 StartZ=0 EndX=4 EndY=4 EndZ=0
    g23: LineSegment [constr] StartX=4 StartY=4 StartZ=0 EndX=4 EndY=116 EndZ=0
    g24: LineSegment [constr] StartX=80 StartY=116 StartZ=0 EndX=80 EndY=118 EndZ=0
    g25: LineSegment [constr] StartX=80 StartY=116 StartZ=0 EndX=82 EndY=116 EndZ=0
    g26: LineSegment [constr] StartX=2 StartY=4 StartZ=0 EndX=4 EndY=4 EndZ=0
    g27: LineSegment [constr] StartX=4 StartY=4 StartZ=0 EndX=4 EndY=2 EndZ=0
  constraints (76):
    c: Horizontal(g1)
    c: Vertical(g0)
    c: Vertical(g2)
    c: Coincident(g4,g3)
    c: Coincident(g2,g3)
    c: Horizontal(g4)
    c: Coincident(g5,g2)
    c: Coincident(g5,g1)
    c: Coincident(g6,g0)
    c: Coincident(g6,g1)
    c: Coincident(g7,g4)
    c: Coincident(g7,g0)
    c: Coincident(g8,g7)
    c: Coincident(g8,g4)
    c: Coincident(g9,g7)
    c: Coincident(g9,g0)
    c: Coincident(g10,g6)
    c: Coincident(g10,g0)
    c: Vertical(g10)
    c: Coincident(g11,g6)
    c: Coincident(g11,g1)
    c: Horizontal(g11)
    c: Coincident(g12,g5)
    c: Coincident(g12,g2)
    c: Coincident(g13,g5)
    c: Coincident(g13,g1)
    c: Horizontal(g13)
    c: Horizontal(g8)
    c: Vertical(g9)
    c: Coincident(g14,g3)
    c: Coincident(g14,g2)
    c: Coincident(g15,g3)
    c: Coincident(g15,g3)
    c: Horizontal(g15)
    c: Vertical(g14)
    c: Distance(g3,g7) = 80
    c: Distance(g3,g5) = 116
    c: Vertical(g12)
    c: Equal(g3,g7)
    c: Equal(g7,g6)
    c: Equal(g6,g5)
    c: Radius(g5) = 7
    c: DistanceY(g-1,g5) = 2
    c: DistanceX(g-1,g5) = 2
    c: Coincident(g20,g21)
    c: Coincident(g21,g22)
    c: Coincident(g22,g23)
    c: Coincident(g23,g20)
    c: Horizontal(g20)
    c: Horizontal(g22)
    c: Vertical(g21)
    c: Vertical(g23)
    c: Coincident(g20,g16)
    c: Coincident(g21,g18)
    c: Coincident(g22,g19)
    c: Coincident(g20,g17)
    c: Radius(g17) = 1.5
    c: Equal(g17,g16)
    c: Equal(g17,g18)
    c: Equal(g17,g19)
    c: Coincident(g24,g17)
    c: PointOnObject(g24,g8)
    c: Coincident(g25,g17)
    c: PointOnObject(g25,g9)
    c: Horizontal(g25)
    c: Vertical(g24)
    c: PointOnObject(g26,g12)
    c: Coincident(g26,g19)
    c: Coincident(g26,g27)
    c: PointOnObject(g27,g13)
    c: Vertical(g27)
    c: Horizontal(g26)
    c: Equal(g26,g27)
    c: Equal(g27,g24)
    c: Equal(g24,g25)
    c: Distance(g26) = 2
FEATURE [PartDesign::Pad] Pad008
  Length = 101
  Length2 = 100
  Placement = pos=(0,0,68) rot=(0,0,1;0rad)
  Reversed = true
  Sketch = -> Sketch010
  Type = 0
FEATURE [Part::Cut] Cut014
  Base = -> Fillet012
  Tool = -> Pad008
FEATURE [Part::Box] Box011  label="Cube011"
  Height = 2.5
  Length = 76
  Placement = pos=(-38,-10,0) rot=(0,0,1;0rad)
  Width = 20
  expr: Placement.Base.y = -Width / 2
  expr: Placement.Base.x = -Length / 2
FEATURE [Part::Box] Box012  label="Cube012"
  Height = 2.5
  Length = 40
  Placement = pos=(-20,-8,1) rot=(0,0,1;0rad)
  Width = 16
  expr: Placement.Base.y = -Width / 2
  expr: Placement.Base.x = -Length / 2
FEATURE [Part::Cut] Cut016
  Base = -> Box011
  Tool = -> Box012
FEATURE [Part::Fillet] Fillet014
  Base = -> Cut016
  Edges = 4 edges r=3: [Edge1,Edge3,Edge6,Edge15]
FEATURE [Part::Cylinder] Cylinder001
  Angle = 360
  Height = 10
  Placement = pos=(-28,0,-2) rot=(0,0,1;0rad)
  Radius = 2.1
FEATURE [Part::Cylinder] Cylinder002
  Angle = 360
  Height = 10
  Placement = pos=(28,0,-2) rot=(0,0,1;0rad)
  Radius = 2.1
FEATURE [Part::MultiFuse] Fusion005
  Shapes = -> [Cylinder001,Cylinder002]
FEATURE [Part::Cut] Cut017
  Base = -> Fillet014
  Tool = -> Fusion005
FEATURE [Sketcher::SketchObject] Sketch011
  Placement = pos=(0,0,0) rot=(1,0,0;1.5708rad)
  sketch-geometry (14):
    g0: LineSegment StartX=-15.5708 StartY=9 StartZ=0 EndX=-3.88447 EndY=9 EndZ=0
    g1: LineSegment StartX=-3.88447 StartY=9 StartZ=0 EndX=1.11553 EndY=14 EndZ=0
    g2: LineSegment StartX=1.11553 StartY=14 StartZ=0 EndX=14.0861 EndY=14 EndZ=0
    g3: LineSegment StartX=14.0861 StartY=14 StartZ=0 EndX=22.4292 EndY=5.65685 EndZ=0
    g4: LineSegment StartX=22.4292 StartY=5.65685 StartZ=0 EndX=22.4292 EndY=0 EndZ=0
    g5: LineSegment StartX=22.4292 StartY=0 StartZ=0 EndX=-15.5708 EndY=0 EndZ=0
    g6: LineSegment StartX=-15.5708 StartY=0 StartZ=0 EndX=-15.5708 EndY=9 EndZ=0
    g7: Circle [constr] CenterX=4.42924 CenterY=6 CenterZ=0 NormalX=0 NormalY=0 NormalZ=1 Radius=2.5
    g8: Circle [constr] CenterX=18.4292 CenterY=4 CenterZ=0 NormalX=0 NormalY=0 NormalZ=1 Radius=1.5
    g9: LineSegment [constr] StartX=18.4292 StartY=4 StartZ=0 EndX=18.4292 EndY=0 EndZ=0
    g10: LineSegment [constr] StartX=18.4292 StartY=4 StartZ=0 EndX=22.4292 EndY=4 EndZ=0
    g11: LineSegment [constr] StartX=4.42924 StartY=6 StartZ=0 EndX=-1.22761 EndY=11.6569 EndZ=0
    g12: LineSegment [constr] StartX=4.42924 StartY=6 StartZ=0 EndX=4.42924 EndY=14 EndZ=0
    g13: LineSegment [constr] StartX=18.4292 StartY=4 StartZ=0 EndX=21.2577 EndY=6.82843 EndZ=0
  constraints (41):
    c: Coincident(g0,g1)
    c: Coincident(g1,g2)
    c: Horizontal(g2)
    c: Coincident(g2,g3)
    c: Coincident(g4,g5)
    c: Horizontal(g5)
    c: Coincident(g5,g6)
    c: Coincident(g6,g0)
    c: Vertical(g6)
    c: Vertical(g4)
    c: Horizontal(g0)
    c: Coincident(g3,g4)
    c: Radius(g7) = 2.5
    c: Radius(g8) = 1.5
    c: Distance(g6) = 9
    c: Distance(g5) = 38
    c: DistanceY(g4,g2) = 14
    c: DistanceX(g7,g8) = 14
    c: Coincident(g9,g8)
    c: PointOnObject(g9,g5)
    c: Vertical(g9)
    c: Coincident(g10,g8)
    c: PointOnObject(g10,g4)
    c: Horizontal(g10)
    c: Equal(g9,g10)
    c: Distance(g9) = 4
    c: PointOnObject(g-1,g5)
    c: Angle(g2,g3) = 2.35619
    c: Angle(g1,g2) = 2.35619
    c: DistanceY(g8,g7) = 2
    c: Coincident(g11,g7)
    c: PointOnObject(g11,g1)
    c: Coincident(g12,g7)
    c: PointOnObject(g12,g2)
    c: Vertical(g12)
    c: Perpendicular(g11,g1)
    c: Equal(g12,g11)
    c: Coincident(g13,g8)
    c: PointOnObject(g13,g3)
    c: Perpendicular(g3,g13)
    c: Equal(g13,g10)
FEATURE [PartDesign::Pad] Pad009
  Length = 20
  Length2 = 100
  Placement = pos=(0,0,0) rot=(1,0,0;1.5708rad)
  Sketch = -> Sketch011
  Type = 0
FEATURE [Sketcher::SketchObject] Sketch012
  Placement = pos=(0,5,0) rot=(1,0,0;1.5708rad)
  sketch-geometry (14):
    g0: LineSegment [constr] StartX=-15.5708 StartY=9 StartZ=0 EndX=-3.88447 EndY=9 EndZ=0
    g1: LineSegment [constr] StartX=-3.88447 StartY=9 StartZ=0 EndX=1.11553 EndY=14 EndZ=0
    g2: LineSegment [constr] StartX=1.11553 StartY=14 StartZ=0 EndX=14.0861 EndY=14 EndZ=0
    g3: LineSegment [constr] StartX=14.0861 StartY=14 StartZ=0 EndX=22.4292 EndY=5.65685 EndZ=0
    g4: LineSegment [constr] StartX=22.4292 StartY=5.65685 StartZ=0 EndX=22.4292 EndY=0 EndZ=0
    g5: LineSegment [constr] StartX=22.4292 StartY=0 StartZ=0 EndX=-15.5708 EndY=0 EndZ=0
    g6: LineSegment [constr] StartX=-15.5708 StartY=0 StartZ=0 EndX=-15.5708 EndY=9 EndZ=0
    g7: Circle CenterX=4.42924 CenterY=6 CenterZ=0 NormalX=0 NormalY=0 NormalZ=1 Radius=2.4
    g8: Circle CenterX=18.4292 CenterY=4 CenterZ=0 NormalX=0 NormalY=0 NormalZ=1 Radius=1.6
    g9: LineSegment [constr] StartX=18.4292 StartY=4 StartZ=0 EndX=18.4292 EndY=0 EndZ=0
    g10: LineSegment [constr] StartX=18.4292 StartY=4 StartZ=0 EndX=22.4292 EndY=4 EndZ=0
    g11: LineSegment [constr] StartX=4.42924 StartY=6 StartZ=0 EndX=-1.22761 EndY=11.6569 EndZ=0
    g12: LineSegment [constr] StartX=4.42924 StartY=6 StartZ=0 EndX=4.42924 EndY=14 EndZ=0
    g13: LineSegment [constr] StartX=18.4292 StartY=4 StartZ=0 EndX=21.2577 EndY=6.82843 EndZ=0
  constraints (41):
    c: Coincident(g0,g1)
    c: Coincident(g1,g2)
    c: Horizontal(g2)
    c: Coincident(g2,g3)
    c: Coincident(g4,g5)
    c: Horizontal(g5)
    c: Coincident(g5,g6)
    c: Coincident(g6,g0)
    c: Vertical(g6)
    c: Vertical(g4)
    c: Horizontal(g0)
    c: Coincident(g3,g4)
    c: Radius(g7) = 2.4
    c: Radius(g8) = 1.6
    c: Distance(g6) = 9
    c: Distance(g5) = 38
    c: DistanceY(g4,g2) = 14
    c: DistanceX(g7,g8) = 14
    c: Coincident(g9,g8)
    c: PointOnObject(g9,g5)
    c: Vertical(g9)
    c: Coincident(g10,g8)
    c: PointOnObject(g10,g4)
    c: Horizontal(g10)
    c: Equal(g9,g10)
    c: Distance(g9) = 4
    c: PointOnObject(g-1,g5)
    c: Angle(g2,g3) = 2.35619
    c: Angle(g1,g2) = 2.35619
    c: DistanceY(g8,g7) = 2
    c: Coincident(g11,g7)
    c: PointOnObject(g11,g1)
    c: Coincident(g12,g7)
    c: PointOnObject(g12,g2)
    c: Vertical(g12)
    c: Perpendicular(g11,g1)
    c: Equal(g12,g11)
    c: Coincident(g13,g8)
    c: PointOnObject(g13,g3)
    c: Perpendicular(g3,g13)
    c: Equal(g13,g10)
FEATURE [Part::Box] Box013  label="Cube013"
  Height = 20
  Length = 30
  Placement = pos=(-5,-16,-2) rot=(0,0,1;0rad)
  Width = 12
FEATURE [Part::Cylinder] Cylinder003
  Angle = 360
  Height = 15
  Placement = pos=(-10.5,-10,-2) rot=(0,0,1;0rad)
  Radius = 1.7
FEATURE [Part::Cut] Cut018
  Base = -> Pad009
  Tool = -> Box013
FEATURE [Part::Prism] Prism
  Circumradius = 3.4
  Height = 10
  Placement = pos=(-10.5,-10,-7) rot=(0,0,1;0rad)
  Polygon = 6
FEATURE [Part::Cut] Cut019
  Base = -> Cut018
  Tool = -> Prism
FEATURE [Part::Cut] Cut020
  Base = -> Cut019
  Tool = -> Cylinder003
FEATURE [Part::Fillet] Fillet015
  Base = -> Cut020
  Edges = 6 edges r=3: [Edge15,Edge17,Edge41,Edge42,Edge43,Edge51]
FEATURE [Part::Fillet] Fillet016
  Base = -> Fillet015
  Edges = 12 edges r=1: [Edge6,Edge8,Edge13,Edge15,Edge17,Edge22,Edge37,Edge39,Edge41,Edge51,Edge62,Edge66]
FEATURE [PartDesign::Pad] Pad010
  Length = 30
  Length2 = 100
  Placement = pos=(0,5,0) rot=(1,0,0;1.5708rad)
  Sketch = -> Sketch012
  Type = 0
FEATURE [Part::Cylinder] Cylinder004
  Angle = 360
  Height = 5
  Placement = pos=(4.5,-0.4,6) rot=(1,0,0;1.5708rad)
  Radius = 4
FEATURE [Part::Cylinder] Cylinder005
  Angle = 360
  Height = 5
  Placement = pos=(4.5,-14.6,6) rot=(1,0,0;1.5708rad)
  Radius = 4
FEATURE [Part::MultiFuse] Fusion006
  Shapes = -> [Cylinder004,Cylinder005]
FEATURE [Part::Chamfer] Chamfer
  Base = -> Fusion006
  Edges = 2 edges r=0.5: [Edge1,Edge6]
FEATURE [Part::MultiFuse] Fusion007
  Shapes = -> [Fillet016,Chamfer]
FEATURE [Part::Cut] Cut021
  Base = -> Fusion007
  Tool = -> Pad010
FEATURE [Mesh::Feature] Eje_Y___Tensor_V3  label="Eje Y - Tensor V3"
  Placement = pos=(0,-2,0) rot=(0,0,1;0rad)
FEATURE [Sketcher::SketchObject] Sketch013
  Placement = pos=(0,0,0) rot=(1,0,0;1.5708rad)
  sketch-geometry (9):
    g0: Circle CenterX=7 CenterY=19 CenterZ=0 NormalX=0 NormalY=0 NormalZ=1 Radius=2.4
    g1: Circle CenterX=22 CenterY=9 CenterZ=0 NormalX=0 NormalY=0 NormalZ=1 Radius=2.4
    g2: ArcOfCircle CenterX=7 CenterY=19 CenterZ=0 NormalX=0 NormalY=0 NormalZ=1 Radius=7 StartAngle=1.08969 EndAngle=4.01639
    g3: LineSegment StartX=10.2393 StartY=25.2054 StartZ=0 EndX=25 EndY=17.5 EndZ=0
    g4: LineSegment StartX=25 StartY=17.5 StartZ=0 EndX=62 EndY=10.5 EndZ=0
    g5: LineSegment StartX=62 StartY=10.5 StartZ=0 EndX=62 EndY=0 EndZ=0
    g6: LineSegment StartX=62 StartY=0 StartZ=0 EndX=18.8235 EndY=0 EndZ=0
    g7: LineSegment StartX=18.8235 StartY=0 StartZ=0 EndX=2.51191 EndY=13.6281 EndZ=0
    g8: LineSegment [constr] StartX=25 StartY=17.5 StartZ=0 EndX=18.8235 EndY=0 EndZ=0
  constraints (26):
    c: Coincident(g3,g4)
    c: Coincident(g4,g5)
    c: PointOnObject(g5,g-1)
    c: Vertical(g5)
    c: Coincident(g5,g6)
    c: Horizontal(g6)
    c: Coincident(g6,g7)
    c: Coincident(g7,g2)
    c: Coincident(g2,g3)
    c: Tangent(g2,g3)
    c: Coincident(g0,g2)
    c: DistanceY(g-1,g0) = 19
    c: DistanceX(g-1,g0) = 7
    c: Radius(g2) = 7
    c: DistanceX(g-1,g1) = 22
    c: DistanceY(g-1,g1) = 9
    c: DistanceY(g-1,g3) = 17.5
    c: DistanceX(g-1,g3) = 25
    c: Coincident(g8,g3)
    c: Coincident(g8,g6)
    c: PointOnObject(g1,g8)
    c: DistanceX(g-1,g5) = 62
    c: Distance(g5) = 10.5
    c: Radius(g0) = 2.4
    c: Radius(g1) = 2.4
    c: Tangent(g2,g7)
FEATURE [PartDesign::Pad] Pad011
  Length = 22
  Length2 = 100
  Placement = pos=(0,0,0) rot=(1,0,0;1.5708rad)
  Reversed = true
  Sketch = -> Sketch013
  Type = 0
FEATURE [Part::Box] Box014  label="Cube014"
  Height = 31
  Length = 36
  Placement = pos=(-1,5,-2) rot=(0,0,1;0rad)
  Width = 12
FEATURE [Part::Cylinder] Cylinder006
  Angle = 360
  Height = 9
  Placement = pos=(22,6.5,9) rot=(-1,0,0;1.5708rad)
  Radius = 9
FEATURE [Part::Cylinder] Cylinder007
  Angle = 360
  Height = 5
  Placement = pos=(22,15.6,9) rot=(-1,0,0;1.5708rad)
  Radius = 4
FEATURE [Part::Cylinder] Cylinder008
  Angle = 360
  Height = 5
  Placement = pos=(22,1.4,9) rot=(-1,0,0;1.5708rad)
  Radius = 4
FEATURE [Part::MultiFuse] Fusion008
  Shapes = -> [Cylinder008,Cylinder007]
FEATURE [Part::Chamfer] Chamfer001
  Base = -> Fusion008
  Edges = 2 edges r=0.5: [Edge3,Edge4]
FEATURE [Part::Cut] Cut022
  Base = -> Box014
  Tool = -> Chamfer001
FEATURE [Part::Cut] Cut023
  Base = -> Pad011
  Tool = -> Cut022
FEATURE [Part::Fillet] Fillet017
  Base = -> Cut023
  Edges = 4 edges r=3: [Edge13,Edge23,Edge25,Edge26]
FEATURE [Part::Fillet] Fillet018
  Base = -> Fillet017
  Edges = 2 edges r=5: [Edge23,Edge33]
FEATURE [Part::Fillet] Fillet019
  Base = -> Fillet018
  Edges = 2 edges r=1: [Edge37,Edge50]
FEATURE [Part::Cone] Cone
  Angle = 360
  Height = 15
  Placement = pos=(53.5,11,-1) rot=(0,0,1;0rad)
  Radius1 = 2.2
  Radius2 = 4
FEATURE [Part::Cut] Cut024
  Base = -> Fillet019
  Tool = -> Cone
FEATURE [Part::Box] Box015  label="Cube015"
  Height = 18
  Length = 18
  Placement = pos=(-2,10,63) rot=(0,0,1;0rad)
  Width = 25
FEATURE [Part::Box] Box016  label="Cube016"
  Height = 16
  Length = 18
  Placement = pos=(0,8,68.5) rot=(0,0,1;0rad)
  Width = 29
FEATURE [Part::Box] Box017  label="Cube017"
  Height = 18
  Length = 18
  Placement = pos=(-2,12,63) rot=(0,0,1;0rad)
  Width = 30
FEATURE [Part::Fillet] Fillet020
  Base = -> Box016
  Edges = 1 edges r=5: [Edge6]
FEATURE [Part::Thickness] Thickness
  Faces = -> Fillet020 [Face7,Face4]
  Intersection = false
  Join = 0
  Mode = 0
  SelfIntersection = false
  Value = -2.1
FEATURE [Part::Cylinder] Cylinder009
  Angle = 360
  Height = 10
  Placement = pos=(-16,-16,0) rot=(0,0,1;0rad)
  Radius = 1.6
FEATURE [Part::Mirroring] Part__Mirroring  label="Cylinder009 (Mirror #1)"
  Base = (0,0,0)
  Normal = (0,1,0)
  Source = -> Cylinder009
FEATURE [Part::Mirroring] Part__Mirroring001  label="Cylinder009 (Mirror #2)"
  Base = (0,0,0)
  Normal = (1,0,0)
  Source = -> Cylinder009
FEATURE [Part::Mirroring] Part__Mirroring002  label="Cylinder009 (Mirror #3)"
  Base = (0,0,0)
  Normal = (1,0,0)
  Source = -> Part__Mirroring
FEATURE [Part::Cylinder] Cylinder010
  Angle = 360
  Height = 10
  Radius = 18
FEATURE [Part::MultiFuse] Fusion009
  Placement = pos=(42,82,64) rot=(0,0,1;0rad)
  Shapes = -> [Cylinder010,Part__Mirroring,Part__Mirroring002,Cylinder009,Part__Mirroring001]
FEATURE [Mesh::Feature] Eje_X___carro_v5rear  label="Eje X - carro v5rear"
  Placement = pos=(-61,22,-38) rot=(0.57735,0.57735,0.57735;2.0944rad)
FEATURE [Mesh::Feature] Eje_X___carro_v5  label="Eje X - carro v5"
  Placement = pos=(1,23.5,-38) rot=(0.57735,-0.57735,-0.57735;2.0944rad)
FEATURE [Part::Feature] Part__Feature004  label="Endstop mec\X\E2nico - Chave fim de curso"
  Placement = pos=(-6.8,0,4) rot=(0.57735,-0.57735,-0.57735;2.0944rad)
  shape: bbox 39.5 x 16 x 1 mm, 17 faces (baked)
FEATURE [Part::Feature] Part__Feature005  label="Endstop mec\X\E2nico - Chave fim de curso001"
  Placement = pos=(-6.8,0,4) rot=(0.57735,-0.57735,-0.57735;2.0944rad)
  shape: bbox 8.748 x 12.4 x 8.1 mm, 174 faces (baked)
FEATURE [Part::Feature] Part__Feature006  label="Endstop mec\X\E2nico - Chave fim de curso002"
  Placement = pos=(-6.8,0,4) rot=(0.57735,-0.57735,-0.57735;2.0944rad)
  shape: bbox 13 x 8.975 x 8 mm, 82 faces (baked)
FEATURE [Part::Feature] Part__Feature007  label="Endstop mec\X\E2nico - Chave fim de curso003"
  Placement = pos=(-6.8,0,4) rot=(0.57735,-0.57735,-0.57735;2.0944rad)
  shape: bbox 15.95 x 2.646 x 3.5 mm, 16 faces (baked)
FEATURE [Part::Feature] Part__Feature008  label="Endstop mec\X\E2nico - Chave fim de curso004"
  Placement = pos=(-6.8,0,4) rot=(0.57735,-0.57735,-0.57735;2.0944rad)
  shape: bbox 33.81 x 4.368 x 0.1 mm, 12 faces (baked)
FEATURE [Part::Feature] Part__Feature009  label="Endstop mec\X\E2nico - Chave fim de curso005"
  Placement = pos=(-6.8,0,4) rot=(0.57735,-0.57735,-0.57735;2.0944rad)
  shape: bbox 7.279 x 4 x 0.1 mm, 15 faces (baked)
FEATURE [Part::Feature] Part__Feature010  label="Endstop mec\X\E2nico - Chave fim de curso006"
  Placement = pos=(-6.8,0,4) rot=(0.57735,-0.57735,-0.57735;2.0944rad)
  shape: bbox 5.25 x 3.5 x 0.1 mm, 11 faces (baked)
FEATURE [Part::Feature] Part__Feature011  label="Endstop mec\X\E2nico - Chave fim de curso007"
  Placement = pos=(-6.8,0,4) rot=(0.57735,-0.57735,-0.57735;2.0944rad)
  shape: bbox 1 x 3.5 x 0.1 mm, 6 faces (baked)
FEATURE [Part::Feature] Part__Feature012  label="Endstop mec\X\E2nico - Chave fim de curso008"
  Placement = pos=(-6.8,0,4) rot=(0.57735,-0.57735,-0.57735;2.0944rad)
  shape: bbox 9 x 3.4 x 0.1 mm, 11 faces (baked)
FEATURE [Part::Feature] Part__Feature013  label="Endstop mec\X\E2nico - Chave fim de curso009"
  Placement = pos=(-6.8,0,4) rot=(0.57735,-0.57735,-0.57735;2.0944rad)
  shape: bbox 26.25 x 9.35 x 0.1 mm, 28 faces (baked)
FEATURE [Part::Feature] Part__Feature014  label="Endstop mec\X\E2nico - Chave fim de curso010"
  Placement = pos=(-6.8,0,4) rot=(0.57735,-0.57735,-0.57735;2.0944rad)
  shape: bbox 21.5 x 7.5 x 0.1 mm, 18 faces (baked)
FEATURE [Part::Feature] Part__Feature015  label="Endstop mec\X\E2nico - Chave fim de curso011"
  Placement = pos=(-6.8,0,4) rot=(0.57735,-0.57735,-0.57735;2.0944rad)
  shape: bbox 0.8165 x 1.6 x 0.8165 mm, 60 faces (baked)
FEATURE [Part::Feature] Part__Feature016  label="Endstop mec\X\E2nico - Chave fim de curso012"
  Placement = pos=(-6.8,0,4) rot=(0.57735,-0.57735,-0.57735;2.0944rad)
  shape: bbox 0.8165 x 1.6 x 0.8165 mm, 60 faces (baked)
FEATURE [Part::Feature] Part__Feature017  label="Endstop mec\X\E2nico - Chave fim de curso013"
  Placement = pos=(-6.8,0,4) rot=(0.57735,-0.57735,-0.57735;2.0944rad)
  shape: bbox 1.6 x 0.8165 x 0.8165 mm, 60 faces (baked)
FEATURE [Part::Feature] Part__Feature018  label="Endstop mec\X\E2nico - Chave fim de curso014"
  Placement = pos=(-6.8,0,4) rot=(0.57735,-0.57735,-0.57735;2.0944rad)
  shape: bbox 1.6 x 0.8165 x 0.8165 mm, 60 faces (baked)
FEATURE [Part::Feature] Part__Feature019  label="E3D_v6_Heat sink"
  Placement = pos=(-11.6635,-16.7611,-30.2119) rot=(1,0,0;1.5708rad)
  shape: bbox 22 x 22 x 42.7 mm, 92 faces (baked)
FEATURE [Part::Feature] Part__Feature020  label="E3D_v6_Heat break"
  Placement = pos=(-11.6635,-16.7611,-37.3119) rot=(1,0,0;1.5708rad)
  shape: bbox 7 x 7 x 22.1 mm, 19 faces (baked)
FEATURE [Part::Feature] Part__Feature021  label="E3D_V6_Heater block"
  Placement = pos=(-11.75,-20.5,-38.0619) rot=(0.578782,0.575916,0.577349;2.0944rad)
  shape: bbox 16.05 x 23.06 x 11.55 mm, 45 faces (baked)
FEATURE [Part::Feature] Part__Feature022  label="E3D_v6_nozzle0.4mm"
  Placement = pos=(-11.7611,-16.8365,-49.8119) rot=(0.57735,-0.57735,-0.57735;2.0944rad)
  shape: bbox 8.083 x 7 x 12.5 mm, 26 faces (baked)
FEATURE [Part::Feature] Part__Feature023  label="BMG_Extruder v3"
  Placement = pos=(-34,-21,21) rot=(0.57735,0.57735,0.57735;2.0944rad)
  shape: bbox 33.6 x 58.2 x 72.95 mm, 276 faces (baked)
FEATURE [Part::Feature] Part__Feature028  label="NEMA_17_SIMPLE_WANTAI v1"
  Placement = pos=(-36,-21,21) rot=(0,0,-1;1.5708rad)
  shape: bbox 66.25 x 42 x 42 mm, 47 faces (baked)
FEATURE [Part::Feature] Part__Feature034  label="M3x0.5 (2)"
  Placement = pos=(-44.5,-36.5,5.5) rot=(0,-1,0;1.5708rad)
  shape: bbox 43.02 x 5.5 x 5.5 mm, 62 faces (baked)
FEATURE [Part::Feature] Part__Feature035  label="M3x0.5 (2)001"
  Placement = pos=(-44.5,-36.5,36.5) rot=(0,-1,0;1.5708rad)
  shape: bbox 43.02 x 5.5 x 5.5 mm, 62 faces (baked)
FEATURE [Part::Feature] Part__Feature036  label="M3x0.5 (2)002"
  Placement = pos=(-44.5,-5.5,5.5) rot=(0,-1,0;1.5708rad)
  shape: bbox 43.02 x 5.5 x 5.5 mm, 62 faces (baked)
FEATURE [App::DocumentObjectGroup] Group  label="endstop"
  Group = -> [Part__Feature004,Part__Feature005,Part__Feature006,Part__Feature007,Part__Feature008,Part__Feature009,Part__Feature010,Part__Feature011,Part__Feature012,Part__Feature013,Part__Feature014,Part__Feature015,Part__Feature016,Part__Feature017,Part__Feature018]
FEATURE [Part::Box] Box018  label="Cube018"
  Height = 44
  Length = 3
  Placement = pos=(-37,-42,-2) rot=(0,0,1;0rad)
  Width = 48
FEATURE [Part::Feature] Part__Feature039  label="NEMA_17_SIMPLE_WANTAI v002"
  Placement = pos=(-36,-21,21) rot=(0,0,-1;1.5708rad)
  shape: bbox 66.25 x 42 x 42 mm, 47 faces (baked)
FEATURE [Part::Box] Box021  label="Cube021"
  Height = 47
  Length = 62
  Placement = pos=(-71,-46,-2) rot=(0,0,1;0rad)
  Width = 50
FEATURE [Part::Cut] Cut028
  Base = -> Part__Feature028
  Placement = pos=(17,0,0) rot=(0,0,1;0rad)
  Tool = -> Box021
FEATURE [Part::Box] Box022  label="Cube022"
  Height = 47
  Length = 70
  Placement = pos=(-125,-46,-2) rot=(0,0,1;0rad)
  Width = 51
FEATURE [Part::Cut] Cut029
  Base = -> Part__Feature039
  Tool = -> Box022
FEATURE [Part::Feature] Part__Feature040  label="turbine"
  Placement = pos=(0,3.2,0) rot=(0,1,0;0.138121rad)
  shape: bbox 38.92 x 10.5 x 38.96 mm, 229 faces (baked)
FEATURE [Part::Feature] Part__Feature041  label="top"
  Placement = pos=(0,15,0) rot=(0,0,1;0rad)
  shape: bbox 51.3 x 8.001 x 51.07 mm, 45 faces (baked)
FEATURE [Part::Feature] Part__Feature042  label="bottom"
  shape: bbox 52.92 x 8.502 x 51.38 mm, 117 faces (baked)
FEATURE [Part::Feature] Part__Feature043  label="bottom001"
  shape: bbox 4.5 x 0.5 x 5.2 mm, 6 faces (baked)
FEATURE [Part::MultiFuse] Fusion012
  Placement = pos=(-29,34,-6) rot=(0,1,0;3.14159rad)
  Shapes = -> [Part__Feature040,Part__Feature041,Part__Feature043,Part__Feature042]
FEATURE [Sketcher::SketchObject] Sketch014
  Placement = pos=(-1.5,4,0) rot=(0.57735,0.57735,0.57735;2.0944rad)
  sketch-geometry (7):
    g0: LineSegment StartX=-10 StartY=-44 StartZ=0 EndX=2.97206 EndY=-38.5 EndZ=0
    g1: LineSegment StartX=2.97206 StartY=-38.5 StartZ=0 EndX=30 EndY=-38.5 EndZ=0
    g2: LineSegment StartX=30 StartY=-38.5 StartZ=0 EndX=30 EndY=-31.5 EndZ=0
    g3: LineSegment StartX=30 StartY=-31.5 StartZ=0 EndX=45 EndY=-31.5 EndZ=0
    g4: LineSegment StartX=45 StartY=-31.5 StartZ=0 EndX=45 EndY=-47 EndZ=0
    g5: LineSegment StartX=45 StartY=-47 StartZ=0 EndX=-6 EndY=-47 EndZ=0
    g6: LineSegment StartX=-10 StartY=-44 StartZ=0 EndX=-6 EndY=-47 EndZ=0
  constraints (16):
    c: Coincident(g0,g1)
    c: Horizontal(g1)
    c: Coincident(g1,g2)
    c: Coincident(g2,g3)
    c: Horizontal(g3)
    c: Coincident(g3,g4)
    c: Horizontal(g5)
    c: Coincident(g5,g4)
    c: Vertical(g2)
    c: Coincident(g6,g0)
    c: Coincident(g6,g5)
    c: DistanceY(g5,g-1) = 47
    c: DistanceX(g-1,g3) = 45
    c: Distance(g3) = 15
    c: Distance(g2) = 7
    c: DistanceY(g2,g-1) = 31.5
FEATURE [PartDesign::Pad] Pad012
  Length = 20
  Length2 = 100
  Placement = pos=(-1.5,4,0) rot=(0.57735,0.57735,0.57735;2.0944rad)
  Reversed = true
  Sketch = -> Sketch014
  Type = 0
FEATURE [Part::MultiFuse] Fusion013
  Placement = pos=(-1,0,0) rot=(0,0,1;0rad)
  Shapes = -> [Cut029,Cut028]
FEATURE [Sketcher::SketchObject] Sketch015
  Placement = pos=(0,8,0) rot=(1,0,0;1.5708rad)
  sketch-geometry (5):
    g0: LineSegment StartX=-26 StartY=42 StartZ=0 EndX=-26 EndY=-16 EndZ=0
    g1: LineSegment StartX=-61 StartY=-3 StartZ=0 EndX=-61 EndY=42 EndZ=0
    g2: LineSegment StartX=-61 StartY=42 StartZ=0 EndX=-26 EndY=42 EndZ=0
    g3: LineSegment StartX=-61 StartY=-3 StartZ=0 EndX=-48 EndY=-16 EndZ=0
    g4: LineSegment StartX=-48 StartY=-16 StartZ=0 EndX=-26 EndY=-16 EndZ=0
  constraints (15):
    c: Vertical(g0)
    c: Vertical(g1)
    c: Coincident(g1,g2)
    c: Horizontal(g2)
    c: Coincident(g1,g3)
    c: Coincident(g3,g4)
    c: Horizontal(g4)
    c: Coincident(g0,g4)
    c: Angle(g4,g3) = 2.35619
    c: Coincident(g0,g2)
    c: DistanceX(g1,g-1) = 61
    c: DistanceY(g1,g-1) = 3
    c: Distance(g1) = 45
    c: DistanceX(g3,g-1) = 48
    c: Distance(g2) = 35
FEATURE [Sketcher::SketchObject] Sketch016
  Placement = pos=(0,0,-3) rot=(0,0,1;0rad)
  sketch-geometry (13):
    g0: LineSegment StartX=-61 StartY=7 StartZ=0 EndX=-61 EndY=-17 EndZ=0
    g1: LineSegment StartX=-61 StartY=-17 StartZ=0 EndX=-40 EndY=-38 EndZ=0
    g2: LineSegment StartX=-40 StartY=-38 StartZ=0 EndX=-26 EndY=-38 EndZ=0
    g3: LineSegment StartX=-26 StartY=-38 StartZ=0 EndX=-26 EndY=7 EndZ=0
    g4: LineSegment StartX=-26 StartY=7 StartZ=0 EndX=-61 EndY=7 EndZ=0
    g5: LineSegment StartX=-50 StartY=-11 StartZ=0 EndX=-37 EndY=-11 EndZ=0
    g6: LineSegment StartX=-37 StartY=-11 StartZ=0 EndX=-37 EndY=-27 EndZ=0
    g7: LineSegment StartX=-37 StartY=-27 StartZ=0 EndX=-40 EndY=-27 EndZ=0
    g8: LineSegment StartX=-50 StartY=-17 StartZ=0 EndX=-50 EndY=-11 EndZ=0
    g9: LineSegment StartX=-50 StartY=-17 StartZ=0 EndX=-40 EndY=-27 EndZ=0
    g10: LineSegment [constr] StartX=-50 StartY=-17 StartZ=0 EndX=-61 EndY=-17 EndZ=0
    g11: LineSegment [constr] StartX=-40 StartY=-27 StartZ=0 EndX=-40 EndY=-38 EndZ=0
    g12: LineSegment [constr] StartX=-37 StartY=-27 StartZ=0 EndX=-26 EndY=-27 EndZ=0
  constraints (39):
    c: Vertical(g0)
    c: Coincident(g0,g1)
    c: Coincident(g1,g2)
    c: Horizontal(g2)
    c: Coincident(g2,g3)
    c: Vertical(g3)
    c: Coincident(g3,g4)
    c: Coincident(g4,g0)
    c: Horizontal(g4)
    c: Horizontal(g5)
    c: Coincident(g5,g6)
    c: Coincident(g6,g7)
    c: Horizontal(g7)
    c: Coincident(g8,g5)
    c: DistanceX(g2,g-1) = 26
    c: DistanceY(g2,g-1) = 38
    c: Angle(g1,g0) = 2.35619
    c: DistanceX(g0,g2) = 35
    c: Coincident(g9,g8)
    c: Coincident(g9,g7)
    c: Vertical(g8)
    c: Parallel(g9,g1)
    c: Coincident(g10,g8)
    c: PointOnObject(g10,g0)
    c: Horizontal(g10)
    c: Coincident(g11,g7)
    c: PointOnObject(g11,g2)
    c: Vertical(g11)
    c: PointOnObject(g12,g3)
    c: Horizontal(g12)
    c: Vertical(g6)
    c: Coincident(g12,g6)
    c: Coincident(g11,g1)
    c: Distance(g2) = 14
    c: Equal(g12,g11)
    c: Equal(g11,g10)
    c: DistanceY(g5,g-1) = 11
    c: Distance(g12) = 11
    c: Distance(g0) = 24
FEATURE [PartDesign::Pad] Pad013
  Length = 3
  Length2 = 100
  Placement = pos=(0,0,-3) rot=(0,0,1;0rad)
  Sketch = -> Sketch016
  Type = 0
FEATURE [PartDesign::Pad] Pad014
  Length = 8
  Length2 = 100
  Placement = pos=(0,8,0) rot=(1,0,0;1.5708rad)
  Sketch = -> Sketch015
  Type = 0
FEATURE [Part::Cylinder] Cylinder011
  Angle = 360
  Height = 25
  Placement = pos=(-30,-8,13.5) rot=(-1,0,0;1.5708rad)
  Radius = 2
FEATURE [Part::Cylinder] Cylinder012
  Angle = 360
  Height = 25
  Placement = pos=(-30,-8,-10) rot=(-1,0,0;1.5708rad)
  Radius = 2
FEATURE [Part::Cylinder] Cylinder013
  Angle = 360
  Height = 25
  Placement = pos=(-57,-8,13.5) rot=(-1,0,0;1.5708rad)
  Radius = 2
FEATURE [Part::Cylinder] Cylinder014
  Angle = 360
  Height = 25
  Placement = pos=(-30,-21,13.5) rot=(-1,0,0;1.5708rad)
  Radius = 3.5
FEATURE [Part::Cylinder] Cylinder015
  Angle = 360
  Height = 25
  Placement = pos=(-30,-21,-10) rot=(-1,0,0;1.5708rad)
  Radius = 3.5
FEATURE [Part::Cylinder] Cylinder016
  Angle = 360
  Height = 25
  Placement = pos=(-57,-21,13.5) rot=(-1,0,0;1.5708rad)
  Radius = 3.5
FEATURE [Part::Cylinder] Cylinder017
  Angle = 360
  Height = 25
  Placement = pos=(-30,-8,38.5) rot=(-1,0,0;1.5708rad)
  Radius = 1.6
FEATURE [Part::Cylinder] Cylinder018
  Angle = 360
  Height = 25
  Placement = pos=(-30,-21,38.5) rot=(-1,0,0;1.5708rad)
  Radius = 2.8
FEATURE [Part::Chamfer] Chamfer003
  Base = -> Box018
  Edges = 2 edges: [Edge9 r=6,Edge10 r=4]
FEATURE [Part::Fillet] Fillet023
  Base = -> Pad014
  Edges = 2 edges r=1: [Edge5,Edge8]
FEATURE [Part::Chamfer] Chamfer004
  Base = -> Fillet023
  Edges = 1 edges r=3: [Edge3]
FEATURE [Part::Cylinder] Cylinder019
  Angle = 360
  Height = 20
  Placement = pos=(0,-5.5,5.5) rot=(0,1,0;1.5708rad)
  Radius = 1.6
FEATURE [Part::Cylinder] Cylinder020
  Angle = 360
  Height = 20
  Placement = pos=(0,-36.5,5.5) rot=(0,1,0;1.5708rad)
  Radius = 1.6
FEATURE [Part::Cylinder] Cylinder021
  Angle = 360
  Height = 20
  Placement = pos=(0,-36.5,36.5) rot=(0,1,0;1.5708rad)
  Radius = 1.6
FEATURE [Part::Cylinder] Cylinder022
  Angle = 360
  Height = 20
  Placement = pos=(0,-5.5,36.5) rot=(0,1,0;1.5708rad)
  Radius = 1.6
FEATURE [Part::Cylinder] Cylinder023
  Angle = 360
  Height = 20
  Placement = pos=(0,-21,21) rot=(0,1,0;1.5708rad)
  Radius = 13
FEATURE [Part::MultiFuse] Fusion020
  Placement = pos=(-49,0,0) rot=(0,0,1;0rad)
  Shapes = -> [Cylinder023,Cylinder019,Cylinder021,Cylinder022,Cylinder020]
FEATURE [Part::Fillet] Fillet024
  Base = -> Pad013
  Edges = 7 edges r=1: [Edge2,Edge5,Edge16,Edge17,Edge20,Edge23,Edge26]
FEATURE [Part::MultiFuse] Fusion022
  Shapes = -> [Cylinder013,Cylinder011,Cylinder012,Cylinder014,Cylinder015,Cylinder016,Cylinder017,Cylinder018]
FEATURE [Part::Box] Box024  label="Cube024"
  Height = 20
  Length = 45
  Placement = pos=(-66,-5,-22) rot=(0,0,1;0rad)
  Width = 10
FEATURE [Part::Cut] Cut030
  Base = -> Chamfer004
  Tool = -> Box024
FEATURE [Part::MultiFuse] Fusion023
  Shapes = -> [Fillet024,Cut030,Chamfer003]
FEATURE [Part::Cut] Cut031
  Base = -> Fusion023
  Tool = -> Fusion020
FEATURE [Part::Cut] Cut032
  Base = -> Cut031
  Tool = -> Fusion022
FEATURE [Part::Chamfer] Chamfer005
  Base = -> Cut032
  Edges = 2 edges r=3: [Edge10,Edge41]
FEATURE [Sketcher::SketchObject] Sketch017
  Placement = pos=(-43.5,6,-11) rot=(1,0,0;1.5708rad)
  sketch-geometry (35):
    g0: LineSegment StartX=-4 StartY=3 StartZ=0 EndX=-2 EndY=3 EndZ=0
    g1: LineSegment StartX=-2 StartY=3 StartZ=0 EndX=-2 EndY=-3 EndZ=0
    g2: LineSegment StartX=-2 StartY=-3 StartZ=0 EndX=-4 EndY=-3 EndZ=0
    g3: LineSegment StartX=-4 StartY=-3 StartZ=0 EndX=-4 EndY=3 EndZ=0
    g4: LineSegment StartX=-1 StartY=-3 StartZ=0 EndX=1 EndY=-3 EndZ=0
    g5: LineSegment StartX=1 StartY=-3 StartZ=0 EndX=1 EndY=-1 EndZ=0
    g6: LineSegment StartX=1 StartY=-1 StartZ=0 EndX=2 EndY=-1 EndZ=0
    g7: LineSegment StartX=2 StartY=-1 StartZ=0 EndX=2 EndY=-3 EndZ=0
    g8: LineSegment StartX=2 StartY=-3 StartZ=0 EndX=4 EndY=-3 EndZ=0
    g9: LineSegment StartX=4 StartY=-3 StartZ=0 EndX=4 EndY=3 EndZ=0
    g10: LineSegment StartX=2 StartY=3 StartZ=0 EndX=2 EndY=1 EndZ=0
    g11: LineSegment StartX=1 StartY=1 StartZ=0 EndX=1 EndY=3 EndZ=0
    g12: LineSegment StartX=1 StartY=3 StartZ=0 EndX=-1 EndY=3 EndZ=0
    g13: LineSegment [constr] StartX=2 StartY=1 StartZ=0 EndX=2 EndY=-1 EndZ=0
    g14: LineSegment StartX=1 StartY=1 StartZ=0 EndX=2 EndY=1 EndZ=0
    g15: LineSegment [constr] StartX=-2 StartY=3 StartZ=0 EndX=-1 EndY=3 EndZ=0
    g16: LineSegment [constr] StartX=1 StartY=3 StartZ=0 EndX=2 EndY=3 EndZ=0
    g17: LineSegment StartX=-1 StartY=3 StartZ=0 EndX=-1 EndY=1 EndZ=0
    g18: LineSegment StartX=-1 StartY=1 StartZ=0 EndX=-1.5 EndY=1 EndZ=0
    g19: LineSegment StartX=-1.5 StartY=1 StartZ=0 EndX=-1.5 EndY=-1 EndZ=0
    g20: LineSegment StartX=-1.5 StartY=-1 StartZ=0 EndX=-1 EndY=-1 EndZ=0
    g21: LineSegment StartX=-1 StartY=-1 StartZ=0 EndX=-1 EndY=-3 EndZ=0
    g22: LineSegment [constr] StartX=-1 StartY=1 StartZ=0 EndX=-1 EndY=-1 EndZ=0
    g23: LineSegment [constr] StartX=-2 StartY=1 StartZ=0 EndX=-1.5 EndY=1 EndZ=0
    g24: LineSegment StartX=2 StartY=3 StartZ=0 EndX=3 EndY=3 EndZ=0
    g25: LineSegment StartX=3 StartY=3 StartZ=0 EndX=4 EndY=3 EndZ=0
    g26: LineSegment [constr] StartX=1 StartY=1 StartZ=0 EndX=1 EndY=-1 EndZ=0
    g27: LineSegment [constr] StartX=-2 StartY=-3 StartZ=0 EndX=-1 EndY=-3 EndZ=0
    g28: Circle CenterX=-3 CenterY=2 CenterZ=0 NormalX=0 NormalY=0 NormalZ=1 Radius=0.5
    g29: LineSegment [constr] StartX=-4 StartY=3 StartZ=0 EndX=-3 EndY=2 EndZ=0
    g30: LineSegment [constr] StartX=-3 StartY=2 StartZ=0 EndX=-2 EndY=3 EndZ=0
    g31: LineSegment [constr] StartX=-4 StartY=2 StartZ=0 EndX=-3.5 EndY=2 EndZ=0
    g32: LineSegment [constr] StartX=-3.5 StartY=2 StartZ=0 EndX=-3 EndY=2 EndZ=0
    g33: LineSegment [constr] StartX=-4 StartY=-3 StartZ=0 EndX=0 EndY=0 EndZ=0
    g34: LineSegment [constr] StartX=0 StartY=0 StartZ=0 EndX=4 EndY=3 EndZ=0
  constraints (95):
    c: Coincident(g0,g1)
    c: Coincident(g1,g2)
    c: Coincident(g2,g3)
    c: Coincident(g3,g0)
    c: Horizontal(g0)
    c: Horizontal(g2)
    c: Vertical(g1)
    c: Vertical(g3)
    c: Horizontal(g4)
    c: Coincident(g4,g5)
    c: Vertical(g5)
    c: Coincident(g5,g6)
    c: Horizontal(g6)
    c: Coincident(g6,g7)
    c: Vertical(g7)
    c: Coincident(g7,g8)
    c: Horizontal(g8)
    c: Coincident(g8,g9)
    c: Vertical(g9)
    c: Vertical(g11)
    c: Coincident(g11,g12)
    c: Horizontal(g12)
    c: Vertical(g10)
    c: Coincident(g13,g6)
    c: Vertical(g13)
    c: Coincident(g13,g10)
    c: Equal(g11,g12)
    c: Equal(g12,g0)
    c: Coincident(g14,g10)
    c: Horizontal(g14)
    c: Coincident(g11,g14)
    c: Coincident(g15,g0)
    c: Equal(g15,g14)
    c: Horizontal(g15)
    c: Coincident(g16,g11)
    c: Horizontal(g16)
    c: Coincident(g12,g17)
    c: Vertical(g17)
    c: Coincident(g17,g18)
    c: Horizontal(g18)
    c: Coincident(g18,g19)
    c: Vertical(g19)
    c: Coincident(g19,g20)
    c: Coincident(g20,g21)
    c: Coincident(g21,g4)
    c: Vertical(g21)
    c: Horizontal(g20)
    c: Coincident(g22,g17)
    c: Coincident(g22,g20)
    c: Vertical(g22)
    c: PointOnObject(g23,g1)
    c: Coincident(g23,g18)
    c: Horizontal(g23)
    c: Equal(g18,g23)
    c: Coincident(g10,g24)
    c: Horizontal(g24)
    c: Coincident(g24,g25)
    c: Coincident(g25,g9)
    c: Horizontal(g25)
    c: Equal(g16,g24)
    c: Equal(g24,g25)
    c: Coincident(g10,g16)
    c: Coincident(g15,g12)
    c: Equal(g17,g11)
    c: Equal(g7,g5)
    c: Equal(g21,g17)
    c: Coincident(g26,g11)
    c: Coincident(g26,g5)
    c: Vertical(g26)
    c: Coincident(g27,g1)
    c: Coincident(g27,g4)
    c: Horizontal(g27)
    c: Equal(g19,g17)
    c: Equal(g26,g11)
    c: Coincident(g29,g0)
    c: Coincident(g29,g28)
    c: Coincident(g30,g28)
    c: Coincident(g30,g0)
    c: Perpendicular(g30,g29)
    c: Equal(g30,g29)
    c: PointOnObject(g31,g3)
    c: PointOnObject(g31,g28)
    c: Coincident(g32,g31)
    c: Coincident(g32,g28)
    c: Horizontal(g31)
    c: Horizontal(g32)
    c: Equal(g31,g32)
    c: Equal(g4,g8)
    c: Distance(g3) = 6
    c: Coincident(g33,g2)
    c: Coincident(g33,g-1)
    c: Coincident(g34,g-1)
    c: Coincident(g34,g9)
    c: Parallel(g34,g33)
    c: Equal(g34,g33)
FEATURE [PartDesign::Pad] Pad015
  Length = 5
  Length2 = 100
  Placement = pos=(-43.5,6,-11) rot=(1,0,0;1.5708rad)
  Sketch = -> Sketch017
  Type = 0
FEATURE [Part::Cut] Cut033
  Base = -> Chamfer005
  Tool = -> Pad015
FEATURE [Part::Fillet] Fillet025
  Base = -> Cut033
  Edges = 1 edges r=1: [Edge31]
FEATURE [Part::Cylinder] Cylinder026
  Angle = 360
  Height = 22
  Placement = pos=(-9,6,1) rot=(1,0,0;1.5708rad)
  Radius = 1.7
FEATURE [Part::Cylinder] Cylinder027
  Angle = 360
  Height = 22
  Placement = pos=(5,6,16.25) rot=(1,0,0;1.5708rad)
  Radius = 1.5
FEATURE [Sketcher::SketchObject] Sketch018
  Placement = pos=(0,2,0) rot=(1,0,0;1.5708rad)
  sketch-geometry (6):
    g0: LineSegment StartX=-13 StartY=20 StartZ=0 EndX=8 EndY=20 EndZ=0
    g1: LineSegment StartX=8 StartY=20 StartZ=0 EndX=8 EndY=-20 EndZ=0
    g2: LineSegment StartX=8 StartY=-20 StartZ=0 EndX=-8 EndY=-20 EndZ=0
    g3: LineSegment StartX=-13 StartY=20 StartZ=0 EndX=-13 EndY=-1 EndZ=0
    g4: LineSegment StartX=-13 StartY=-1 StartZ=0 EndX=-8 EndY=-6 EndZ=0
    g5: LineSegment StartX=-8 StartY=-6 StartZ=0 EndX=-8 EndY=-20 EndZ=0
  constraints (18):
    c: Coincident(g0,g1)
    c: Vertical(g1)
    c: Horizontal(g0)
    c: Horizontal(g2)
    c: Coincident(g1,g2)
    c: Distance(g1) = 40
    c: Coincident(g0,g3)
    c: Vertical(g3)
    c: Distance(g2) = 16
    c: Coincident(g3,g4)
    c: Coincident(g4,g5)
    c: Coincident(g5,g2)
    c: Vertical(g5)
    c: Distance(g3) = 21
    c: Distance(g5) = 14
    c: Distance(g0) = 21
    c: DistanceY(g-1,g0) = 20
    c: DistanceX(g-1,g0) = 8
FEATURE [PartDesign::Pad] Pad016
  Length = 12
  Length2 = 100
  Placement = pos=(0,2,0) rot=(1,0,0;1.5708rad)
  Sketch = -> Sketch018
  Type = 0
FEATURE [Part::Box] Box025  label="Cube025"
  Height = 44
  Length = 20
  Placement = pos=(-8,0,-22) rot=(0,0,1;0rad)
  Width = 10
FEATURE [Part::Cylinder] Cylinder028
  Angle = 360
  Height = 22
  Placement = pos=(1,6,1) rot=(1,0,0;1.5708rad)
  Radius = 1.7
FEATURE [Part::Cylinder] Cylinder029
  Angle = 360
  Height = 22
  Placement = pos=(5,6,-2.75) rot=(1,0,0;1.5708rad)
  Radius = 1.5
FEATURE [Part::Cylinder] Cylinder030
  Angle = 360
  Height = 22
  Placement = pos=(1,15,1) rot=(1,0,0;1.5708rad)
  Radius = 2.8
FEATURE [Part::Cylinder] Cylinder031
  Angle = 360
  Height = 22
  Placement = pos=(-9,15,1) rot=(1,0,0;1.5708rad)
  Radius = 2.8
FEATURE [Part::MultiFuse] Fusion024
  Shapes = -> [Cylinder030,Cylinder031,Cylinder027,Cylinder029,Cylinder026,Cylinder028]
FEATURE [Part::Cut] Cut034
  Base = -> Pad016
  Tool = -> Fusion024
FEATURE [Part::Box] Box026  label="Cube026"
  Height = 14
  Length = 4
  Placement = pos=(-2.5,-3,0) rot=(0,0,1;0rad)
  Width = 10
FEATURE [Part::Box] Box027  label="Cube027"
  Height = 4
  Length = 10.75
  Placement = pos=(-5,-3,-10.5) rot=(0,0,1;0rad)
  Width = 10
FEATURE [Part::MultiFuse] Fusion025
  Shapes = -> [Box026,Box027]
FEATURE [Part::Cut] Cut035
  Base = -> Cut034
  Tool = -> Fusion025
FEATURE [Part::Cut] Cut036
  Base = -> Cut035
  Tool = -> Box025
FEATURE [Part::Box] Box028  label="Cube028"
  Height = 10
  Length = 61
  Placement = pos=(-71,35,32) rot=(0,0,1;0rad)
  Width = 3
FEATURE [Part::Box] Box029  label="Cube029"
  Height = 22
  Length = 3
  Placement = pos=(-73,35,20) rot=(0,0,1;0rad)
  Width = 10
FEATURE [Part::Box] Box030  label="Cube030"
  Height = 21
  Length = 26
  Placement = pos=(-71,35,20) rot=(0,0,1;0rad)
  Width = 3
FEATURE [Part::Chamfer] Chamfer006
  Base = -> Box030
  Edges = 1 edges r=12: [Edge8]
FEATURE [Part::Box] Box031  label="Cube031"
  Height = 22
  Length = 4
  Placement = pos=(-61,30,20) rot=(0,0,1;0rad)
  Width = 7
FEATURE [Part::MultiFuse] Fusion026
  Shapes = -> [Box028,Chamfer006]
FEATURE [Part::MultiFuse] Fusion027
  Shapes = -> [Fusion026,Box031]
FEATURE [Part::MultiFuse] Fusion028
  Shapes = -> [Fusion027,Box029]
FEATURE [Part::Cylinder] Cylinder032
  Angle = 360
  Height = 10
  Placement = pos=(-44.5,30,38.5) rot=(-1,0,0;1.5708rad)
  Radius = 1.6
FEATURE [Part::Cylinder] Cylinder033
  Angle = 360
  Height = 10
  Placement = pos=(-15.5,30,38.5) rot=(-1,0,0;1.5708rad)
  Radius = 1.6
FEATURE [Part::MultiFuse] Fusion029
  Shapes = -> [Cylinder032,Cylinder033]
FEATURE [Part::Chamfer] Chamfer007
  Base = -> Fusion028
  Edges = 1 edges r=3: [Edge31]
FEATURE [Part::Cut] Cut037
  Base = -> Chamfer007
  Tool = -> Fusion029
FEATURE [Part::Fillet] Fillet026
  Base = -> Cut037
  Edges = 2 edges r=1: [Edge35,Edge39]
FEATURE [Mesh::Feature] Eje_Z___Soporte_Endstop_Eje_Z  label="Eje Z - Soporte Endstop Eje Z"
FEATURE [Sketcher::SketchObject] Sketch019
  Placement = pos=(0,30,0) rot=(0,0.707107,0.707107;3.14159rad)
  sketch-geometry (16):
    g0: Circle CenterX=6 CenterY=14 CenterZ=0 NormalX=0 NormalY=0 NormalZ=1 Radius=1.5
    g1: Circle CenterX=49 CenterY=-24 CenterZ=0 NormalX=0 NormalY=0 NormalZ=1 Radius=1.5
    g2: ArcOfCircle CenterX=6 CenterY=14 CenterZ=0 NormalX=0 NormalY=0 NormalZ=1 Radius=3.5 StartAngle=0.847053 EndAngle=3.14159
    g3: ArcOfCircle CenterX=49 CenterY=-24 CenterZ=0 NormalX=0 NormalY=0 NormalZ=1 Radius=3.5 StartAngle=4.71239 EndAngle=7.13023
    g4: LineSegment StartX=48 StartY=-27.5 StartZ=0 EndX=48 EndY=-38 EndZ=0
    g5: LineSegment StartX=48 StartY=-38 StartZ=0 EndX=-6 EndY=-38 EndZ=0
    g6: LineSegment StartX=12 StartY=-3.7 StartZ=0 EndX=2.5 EndY=5.8 EndZ=0
    g7: LineSegment StartX=2.5 StartY=5.8 StartZ=0 EndX=2.5 EndY=14 EndZ=0
    g8: LineSegment StartX=8.31768 StartY=16.6227 StartZ=0 EndX=51.3177 EndY=-21.3773 EndZ=0
    g9: LineSegment StartX=48 StartY=-27.5 StartZ=0 EndX=49 EndY=-27.5 EndZ=0
    g10: Circle CenterX=20.7 CenterY=-35.85 CenterZ=0 NormalX=0 NormalY=0 NormalZ=1 Radius=1.5
    g11: Circle CenterX=20.7 CenterY=-8.2 CenterZ=0 NormalX=0 NormalY=0 NormalZ=1 Radius=1.5
    g12: LineSegment [constr] StartX=20.7 StartY=-8.2 StartZ=0 EndX=20.7 EndY=-35.85 EndZ=0
    g13: LineSegment StartX=12 StartY=-3.7 StartZ=0 EndX=12 EndY=-31.5 EndZ=0
    g14: LineSegment StartX=12 StartY=-31.5 StartZ=0 EndX=-6 EndY=-31.5 EndZ=0
    g15: LineSegment StartX=-6 StartY=-31.5 StartZ=0 EndX=-6 EndY=-38 EndZ=0
  constraints (47):
    c: Coincident(g2,g0)
    c: Vertical(g4)
    c: Coincident(g4,g5)
    c: Horizontal(g5)
    c: Coincident(g6,g7)
    c: Coincident(g7,g2)
    c: Vertical(g7)
    c: Tangent(g2,g7)
    c: DistanceX(g-1,g0) = 6
    c: DistanceY(g-1,g0) = 14
    c: DistanceY(g1,g-1) = 24
    c: DistanceX(g-1,g1) = 49
    c: Coincident(g8,g2)
    c: Coincident(g8,g3)
    c: Coincident(g9,g4)
    c: Coincident(g9,g3)
    c: Horizontal(g9)
    c: Tangent(g9,g3)
    c: Coincident(g3,g1)
    c: Equal(g3,g2)
    c: Radius(g3) = 3.5
    c: Radius(g1) = 1.5
    c: Equal(g1,g0)
    c: DistanceY(g4,g4) = 10.5
    c: Tangent(g2,g8)
    c: Tangent(g8,g3)
    c: Coincident(g12,g11)
    c: Coincident(g12,g10)
    c: Vertical(g12)
    c: DistanceY(g10,g-1) = 35.85
    c: DistanceX(g-1,g10) = 20.7
    c: Distance(g12) = 27.65
    c: Radius(g11) = 1.5
    c: Equal(g11,g10)
    c: DistanceY(g6,g-1) = 3.7
    c: Coincident(g6,g13)
    c: Vertical(g13)
    c: Coincident(g13,g14)
    c: Horizontal(g14)
    c: Coincident(g14,g15)
    c: Vertical(g15)
    c: DistanceX(g-1,g6) = 12
    c: Coincident(g5,g15)
    c: Distance(g15) = 6.5
    c: Distance(g5) = 54
    c: DistanceX(g-1,g4) = 48
    c: Angle(g6,g13) = 2.35619
FEATURE [PartDesign::Pad] Pad017
  Length = 4
  Length2 = 100
  Placement = pos=(0,30,0) rot=(0,0.707107,0.707107;3.14159rad)
  Sketch = -> Sketch019
  Type = 0
FEATURE [Part::Box] Box032  label="Cube032"
  Height = 6.5
  Length = 7.25
  Placement = pos=(-1.25,33,-38) rot=(0,0,1;0rad)
  Width = 12
FEATURE [Part::Box] Box033  label="Cube033"
  Height = 6.5
  Length = 7.25
  Placement = pos=(-29,33,-38) rot=(0,0,1;0rad)
  Width = 12
FEATURE [Part::MultiFuse] Fusion030
  Shapes = -> [Pad017,Box033,Box032]
FEATURE [Part::Fillet] Fillet027
  Base = -> Fusion030
  Edges = 4 edges r=1: [Edge46,Edge49,Edge68,Edge69]
FEATURE [Part::Cylinder] Cylinder034
  Angle = 360
  Height = 30
  Placement = pos=(2,27,-34.75) rot=(-1,0,0;1.5708rad)
  Radius = 1.5
FEATURE [Part::Cylinder] Cylinder035
  Angle = 360
  Height = 30
  Placement = pos=(-25,27,-34.75) rot=(-1,0,0;1.5708rad)
  Radius = 1.5
FEATURE [Part::MultiFuse] Fusion031
  Shapes = -> [Cylinder034,Cylinder035]
FEATURE [Part::Cut] Cut038
  Base = -> Fillet027
  Tool = -> Fusion031
FEATURE [Part::Chamfer] Chamfer008
  Base = -> Cut038
  Edges = 1 edges r=3: [Edge12]
FEATURE [App::DocumentObjectGroup] Group001  label="x_carriage"
  Group = -> [Fusion012,Fusion013,Fillet025,Part__Feature019,Part__Feature020,Part__Feature021,Part__Feature022,Part__Feature023,Part__Feature034,Part__Feature035,Part__Feature036,Eje_X___carro_v5rear,Eje_X___carro_v5,Fillet026,Chamfer008]
FEATURE [Part::Box] Box034  label="Cube034"
  Height = 6.5
  Length = 8.25
  Placement = pos=(-29,45,-38) rot=(0,0,1;0rad)
  Width = 4
FEATURE [Part::Box] Box035  label="Cube035"
  Height = 6.5
  Length = 8.25
  Placement = pos=(-2.25,45,-38) rot=(0,0,1;0rad)
  Width = 4
FEATURE [Part::Cylinder] Cylinder036
  Angle = 360
  Height = 30
  Placement = pos=(2,27,-34.75) rot=(-1,0,0;1.5708rad)
  Radius = 1.6
FEATURE [Part::Cylinder] Cylinder037
  Angle = 360
  Height = 30
  Placement = pos=(-25,27,-34.75) rot=(-1,0,0;1.5708rad)
  Radius = 1.6
FEATURE [Part::MultiFuse] Fusion032
  Shapes = -> [Box035,Box034]
FEATURE [Part::MultiFuse] Fusion033
  Shapes = -> [Cylinder036,Cylinder037]
FEATURE [Part::Cut] Cut039
  Base = -> Fusion032
  Tool = -> Fusion033
FEATURE [Part::Fillet] Fillet028
  Base = -> Cut039
  Edges = 4 edges r=1: [Edge10,Edge14,Edge17,Edge19]
FEATURE [Part::Box] Box036  label="Cube036"
  Height = 3
  Length = 16.6
  Placement = pos=(-19.8,35.3,-32) rot=(0,0,1;0rad)
  Width = 12.4
FEATURE [Part::Box] Box037  label="Cube037"
  Height = 12
  Length = 14.6
  Placement = pos=(-18.8,36.3,-39) rot=(0,0,1;0rad)
  Width = 10.4
FEATURE [Part::Fillet] Fillet029
  Base = -> Pad012
  Edges = 2 edges: [Edge5 r=0.2,Edge14 r=9]
FEATURE [Part::Thickness] Thickness001
  Faces = -> Fillet029 [Face7]
  Intersection = false
  Join = 0
  Mode = 0
  SelfIntersection = false
  Value = -1.2
FEATURE [Part::MultiFuse] Fusion034
  Shapes = -> [Thickness001,Box036]
FEATURE [Part::Cut] Cut040
  Base = -> Fusion034
  Tool = -> Box037
FEATURE [Part::Chamfer] Chamfer009
  Base = -> Cut040
  Edges = 2 edges: [Edge24 r=0.5,Edge26 r=1]
FEATURE [Part::MultiFuse] Fusion035
  Shapes = -> [Chamfer009,Fillet028]
FEATURE [Part::Fillet] Fillet030
  Base = -> Fusion035
  Edges = 7 edges r=1: [Edge47,Edge49,Edge56,Edge57,Edge58,Edge59,Edge66]
FEATURE [Part::Chamfer] Chamfer010
  Base = -> Fillet030
  Edges = 1 edges r=0.3: [Edge54]
FEATURE [Sketcher::SketchObject] Sketch020
  sketch-geometry (11):
    g0: LineSegment StartX=-15.5348 StartY=18.4475 StartZ=0 EndX=-6.35512 EndY=18.4475 EndZ=0
    g1: LineSegment StartX=-6.35512 StartY=18.4475 StartZ=0 EndX=-6.35512 EndY=26.2149 EndZ=0
    g2: LineSegment StartX=-6.35512 StartY=26.2149 StartZ=0 EndX=-15.5348 EndY=26.2149 EndZ=0
    g3: LineSegment StartX=-15.5348 StartY=26.2149 StartZ=0 EndX=-15.5348 EndY=18.4475 EndZ=0
    g4: LineSegment StartX=-8 StartY=-12.9826 StartZ=0 EndX=-8 EndY=3.85484 EndZ=0
    g5: LineSegment StartX=-8 StartY=3.85484 StartZ=0 EndX=-18.6096 EndY=3.85484 EndZ=0
    g6: LineSegment StartX=-18.6096 StartY=3.85484 StartZ=0 EndX=-18.6096 EndY=8.01744 EndZ=0
    g7: LineSegment StartX=-18.6096 StartY=8.01744 StartZ=0 EndX=8 EndY=8.01744 EndZ=0
    g8: LineSegment StartX=8 StartY=8.01744 StartZ=0 EndX=8 EndY=-12.9826 EndZ=0
    g9: Circle CenterX=0 CenterY=0 CenterZ=0 NormalX=0 NormalY=0 NormalZ=1 Radius=5.13178
    g10: LineSegment StartX=-8 StartY=-12.9826 StartZ=0 EndX=8 EndY=-12.9826 EndZ=0
  constraints (23):
    c: Coincident(g0,g1)
    c: Coincident(g1,g2)
    c: Coincident(g2,g3)
    c: Coincident(g3,g0)
    c: Horizontal(g0)
    c: Horizontal(g2)
    c: Vertical(g1)
    c: Vertical(g3)
    c: Vertical(g4)
    c: Coincident(g4,g5)
    c: Horizontal(g5)
    c: Coincident(g5,g6)
    c: Vertical(g6)
    c: Coincident(g6,g7)
    c: Horizontal(g7)
    c: Coincident(g7,g8)
    c: Vertical(g8)
    c: Distance(g4,g8) = 16
    c: Distance(g8) = 21
    c: Coincident(g9,g-1)
    c: Coincident(g10,g4)
    c: Coincident(g10,g8)
    c: Horizontal(g10)
FEATURE [Sketcher::SketchObject] Sketch021
  sketch-geometry (6):
    g0: LineSegment StartX=-26.8 StartY=8 StartZ=0 EndX=13.2 EndY=8 EndZ=0
    g1: LineSegment StartX=13.2 StartY=8 StartZ=0 EndX=13.2 EndY=-8 EndZ=0
    g2: LineSegment StartX=13.2 StartY=-8 StartZ=0 EndX=-26.8 EndY=-8 EndZ=0
    g3: LineSegment StartX=-26.8 StartY=-8 StartZ=0 EndX=-26.8 EndY=8 EndZ=0
    g4: Circle CenterX=-9.5 CenterY=5 CenterZ=0 NormalX=0 NormalY=0 NormalZ=1 Radius=1.4
    g5: Circle CenterX=9.5 CenterY=5 CenterZ=0 NormalX=0 NormalY=0 NormalZ=1 Radius=1.4
  constraints (17):
    c: Coincident(g0,g1)
    c: Coincident(g1,g2)
    c: Coincident(g2,g3)
    c: Coincident(g3,g0)
    c: Horizontal(g0)
    c: Horizontal(g2)
    c: Vertical(g1)
    c: Vertical(g3)
    c: Radius(g4) = 1.4
    c: Equal(g4,g5)
    c: Distance(g0) = 40
    c: Distance(g3) = 16
    c: DistanceY(g2,g-1) = 8
    c: DistanceY(g-1,g4) = 5
    c: Distance(g4,g5) = 19
    c: DistanceX(g0,g4) = 17.3
    c: Symmetric(g4,g5,g-2)
FEATURE [PartDesign::Pad] Pad018
  Length = 3
  Length2 = 100
  Sketch = -> Sketch021
  Type = 0
FEATURE [Part::Cylinder] Cylinder038
  Angle = 360
  Height = 100
  Placement = pos=(0,-50,-5) rot=(-1,0,0;1.5708rad)
  Radius = 5
  expr: Placement.Base.y = -Height / 2
FEATURE [Sketcher::SketchObject] Sketch022
  Placement = pos=(0,8,0) rot=(1,0,0;1.5708rad)
  sketch-geometry (10):
    g0: LineSegment StartX=-8 StartY=-16 StartZ=0 EndX=-8 EndY=3 EndZ=0
    g1: LineSegment StartX=-8 StartY=3 StartZ=0 EndX=8 EndY=3 EndZ=0
    g2: LineSegment StartX=8 StartY=3 StartZ=0 EndX=8 EndY=-16 EndZ=0
    g3: LineSegment StartX=8 StartY=-16 StartZ=0 EndX=4.5 EndY=-16 EndZ=0
    g4: LineSegment StartX=4.5 StartY=-16 StartZ=0 EndX=4.5 EndY=-7.17945 EndZ=0
    g5: LineSegment [constr] StartX=4.5 StartY=-7.17945 StartZ=0 EndX=-4.5 EndY=-7.17945 EndZ=0
    g6: LineSegment StartX=-4.5 StartY=-7.17945 StartZ=0 EndX=-4.5 EndY=-16 EndZ=0
    g7: LineSegment StartX=-4.5 StartY=-16 StartZ=0 EndX=-8 EndY=-16 EndZ=0
    g8: LineSegment [constr] StartX=-4.5 StartY=-16 StartZ=0 EndX=4.5 EndY=-16 EndZ=0
    g9: ArcOfCircle CenterX=0 CenterY=-5 CenterZ=0 NormalX=0 NormalY=0 NormalZ=1 Radius=5 StartAngle=5.83216 EndAngle=9.8758
  constraints (29):
    c: Vertical(g0)
    c: Coincident(g0,g1)
    c: Horizontal(g1)
    c: Coincident(g1,g2)
    c: Vertical(g2)
    c: Coincident(g2,g3)
    c: Horizontal(g3)
    c: Coincident(g3,g4)
    c: Vertical(g4)
    c: Coincident(g4,g5)
    c: Horizontal(g5)
    c: Coincident(g5,g6)
    c: Vertical(g6)
    c: Coincident(g6,g7)
    c: Coincident(g0,g7)
    c: Horizontal(g7)
    c: Coincident(g8,g6)
    c: Horizontal(g8)
    c: PointOnObject(g9,g-2)
    c: Coincident(g9,g5)
    c: Coincident(g9,g4)
    c: Radius(g9) = 5
    c: Distance(g0,g2) = 16
    c: Coincident(g3,g8)
    c: Distance(g-1,g9) = 5
    c: Equal(g3,g7)
    c: Distance(g3) = 3.5
    c: DistanceY(g-1,g1) = 3
    c: Distance(g0) = 19
FEATURE [PartDesign::Pad] Pad019
  Length = 34
  Length2 = 100
  Placement = pos=(0,8,0) rot=(1,0,0;1.5708rad)
  Sketch = -> Sketch022
  Type = 0
FEATURE [Part::Fillet] Fillet031
  Base = -> Pad019
  Edges = 2 edges r=7: [Edge2,Edge5]
FEATURE [Part::Fillet] Fillet032
  Base = -> Fillet031
  Edges = 4 edges r=3: [Edge6,Edge13,Edge17,Edge24]
FEATURE [Part::MultiFuse] Fusion036
  Shapes = -> [Pad018,Fillet032]
FEATURE [Part::Cylinder] Cylinder039
  Angle = 360
  Height = 28
  Placement = pos=(-12,1,-12) rot=(0,1,0;1.5708rad)
  Radius = 1.5
FEATURE [Part::Cylinder] Cylinder040
  Angle = 360
  Height = 28
  Placement = pos=(-16,-19,-12) rot=(0.250563,0.935113,0.250563;1.63783rad)
  Radius = 1.5
FEATURE [Part::Prism] Prism001
  Circumradius = 3.2
  Height = 10
  Placement = pos=(-16,-19,-12) rot=(0.250563,0.935113,0.250563;1.63783rad)
  Polygon = 6
FEATURE [Part::Prism] Prism002
  Circumradius = 3.2
  Height = 10
  Placement = pos=(-16,1,-12) rot=(0.250563,0.935113,0.250563;1.63783rad)
  Polygon = 6
FEATURE [Part::MultiFuse] Fusion037
  Shapes = -> [Prism002,Prism001,Cylinder040,Cylinder039]
FEATURE [Part::Cut] Cut041
  Base = -> Fusion036
  Tool = -> Fusion037
FEATURE [Part::Fillet] Fillet033
  Base = -> Cut041
  Edges = 6 edges r=0.5: [Edge1,Edge2,Edge10,Edge22,Edge33,Edge36]
FEATURE [Part::Box] Box038  label="Cube038"
  Height = 14
  Length = 4
  Placement = pos=(-2.5,-3,0) rot=(0,0,1;0rad)
  Width = 10
FEATURE [Part::Box] Box039  label="Cube039"
  Height = 4
  Length = 10.75
  Placement = pos=(-5,-3,-10.5) rot=(0,0,1;0rad)
  Width = 10
FEATURE [Part::MultiFuse] Fusion038
  Placement = pos=(-7,0,5) rot=(0.57735,0.57735,0.57735;2.0944rad)
  Shapes = -> [Box038,Box039]
FEATURE [Part::Cut] Cut042
  Base = -> Fillet033
  Tool = -> Fusion038
FEATURE [Part::Cut] Cut043
  Base = -> Cut014
  Tool = -> Box015
FEATURE [Part::Cylinder] Cylinder041
  Angle = 360
  Height = 10
  Placement = pos=(-16,-16,0) rot=(0,0,1;0rad)
  Radius = 1.6
FEATURE [Part::Mirroring] Part__Mirroring003  label="Cylinder009 (Mirror #1)001"
  Base = (0,0,0)
  Normal = (0,1,0)
  Source = -> Cylinder041
FEATURE [Part::Mirroring] Part__Mirroring004  label="Cylinder009 (Mirror #2)001"
  Base = (0,0,0)
  Normal = (1,0,0)
  Source = -> Cylinder041
FEATURE [Part::Mirroring] Part__Mirroring005  label="Cylinder009 (Mirror #3)001"
  Base = (0,0,0)
  Normal = (1,0,0)
  Source = -> Part__Mirroring003
FEATURE [Part::Cylinder] Cylinder042
  Angle = 360
  Height = 10
  Radius = 18
FEATURE [Part::MultiFuse] Fusion040
  Placement = pos=(42,40,64) rot=(0,0,1;0rad)
  Shapes = -> [Cylinder042,Part__Mirroring003,Part__Mirroring005,Cylinder041,Part__Mirroring004]
FEATURE [Part::MultiFuse] Fusion041
  Placement = pos=(8,-1,0) rot=(0,0,1;0rad)
  Shapes = -> [Fusion009,Fusion040]
FEATURE [Sketcher::SketchObject] Sketch023
  sketch-geometry (14):
    g0: ArcOfCircle CenterX=0 CenterY=0 CenterZ=0 NormalX=0 NormalY=0 NormalZ=1 Radius=5 StartAngle=1.98231 EndAngle=7.44246
    g1: ArcOfCircle CenterX=0 CenterY=0 CenterZ=0 NormalX=0 NormalY=0 NormalZ=1 Radius=6.5 StartAngle=2.05052 EndAngle=7.37425
    g2: LineSegment StartX=-3 StartY=5.76628 StartZ=0 EndX=-3 EndY=6.76628 EndZ=0
    g3: LineSegment StartX=-3 StartY=6.76628 StartZ=0 EndX=-4.5 EndY=6.76628 EndZ=0
    g4: LineSegment StartX=-4.5 StartY=6.76628 StartZ=0 EndX=-4.5 EndY=8.26628 EndZ=0
    g5: LineSegment StartX=-4.5 StartY=8.26628 StartZ=0 EndX=-2 EndY=8.26628 EndZ=0
    g6: LineSegment StartX=-2 StartY=8.26628 StartZ=0 EndX=-2 EndY=4.58258 EndZ=0
    g7: LineSegment StartX=2 StartY=4.58258 StartZ=0 EndX=2 EndY=8.26628 EndZ=0
    g8: LineSegment StartX=2 StartY=8.26628 StartZ=0 EndX=4.5 EndY=8.26628 EndZ=0
    g9: LineSegment StartX=4.5 StartY=8.26628 StartZ=0 EndX=4.5 EndY=6.76628 EndZ=0
    g10: LineSegment StartX=4.5 StartY=6.76628 StartZ=0 EndX=3 EndY=6.76628 EndZ=0
    g11: LineSegment StartX=3 StartY=6.76628 StartZ=0 EndX=3 EndY=5.76628 EndZ=0
    g12: LineSegment [constr] StartX=-2 StartY=4.58258 StartZ=0 EndX=2 EndY=4.58258 EndZ=0
    g13: LineSegment [constr] StartX=-2 StartY=8.26628 StartZ=0 EndX=2 EndY=8.26628 EndZ=0
  constraints (40):
    c: Coincident(g0,g-1)
    c: Coincident(g1,g-1)
    c: Vertical(g2)
    c: Coincident(g2,g3)
    c: Horizontal(g3)
    c: Coincident(g3,g4)
    c: Vertical(g4)
    c: Coincident(g4,g5)
    c: Horizontal(g5)
    c: Coincident(g5,g6)
    c: Vertical(g6)
    c: Coincident(g0,g6)
    c: Coincident(g2,g1)
    c: Coincident(g7,g8)
    c: Horizontal(g8)
    c: Coincident(g8,g9)
    c: Vertical(g9)
    c: Coincident(g9,g10)
    c: Horizontal(g10)
    c: Coincident(g10,g11)
    c: Vertical(g11)
    c: Coincident(g1,g11)
    c: Coincident(g7,g0)
    c: Vertical(g7)
    c: Coincident(g12,g0)
    c: Coincident(g12,g0)
    c: Horizontal(g12)
    c: Coincident(g13,g5)
    c: Coincident(g13,g7)
    c: Horizontal(g13)
    c: Equal(g5,g8)
    c: Distance(g4) = 1.5
    c: Distance(g5) = 2.5
    c: Equal(g3,g10)
    c: Radius(g0) = 5
    c: Radius(g1) = 6.5
    c: Distance(g12) = 4
    c: Distance(g1,g1) = 6
    c: Distance(g2) = 1
    c: Equal(g9,g4)
FEATURE [PartDesign::Pad] Pad020
  Length = 10
  Length2 = 100
  Sketch = -> Sketch023
  Type = 0
FEATURE [Part::Chamfer] Chamfer011
  Base = -> Pad020
  Edges = 2 edges r=0.7: [Edge8,Edge23]
FEATURE [Part::MultiFuse] Fusion042
  Shapes = -> [Cut043,Thickness]
FEATURE [Part::Cut] Cut044
  Base = -> Fusion042
  Tool = -> Fusion041
FEATURE [Part::Cut] Cut045
  Base = -> Cut044
  Tool = -> Pad007
FEATURE [Part::Fillet] Fillet034
  Base = -> Cut045
  Edges = 8 edges r=1: [Edge20,Edge21,Edge22,Edge33,Edge38,Edge68,Edge86,Edge87]
